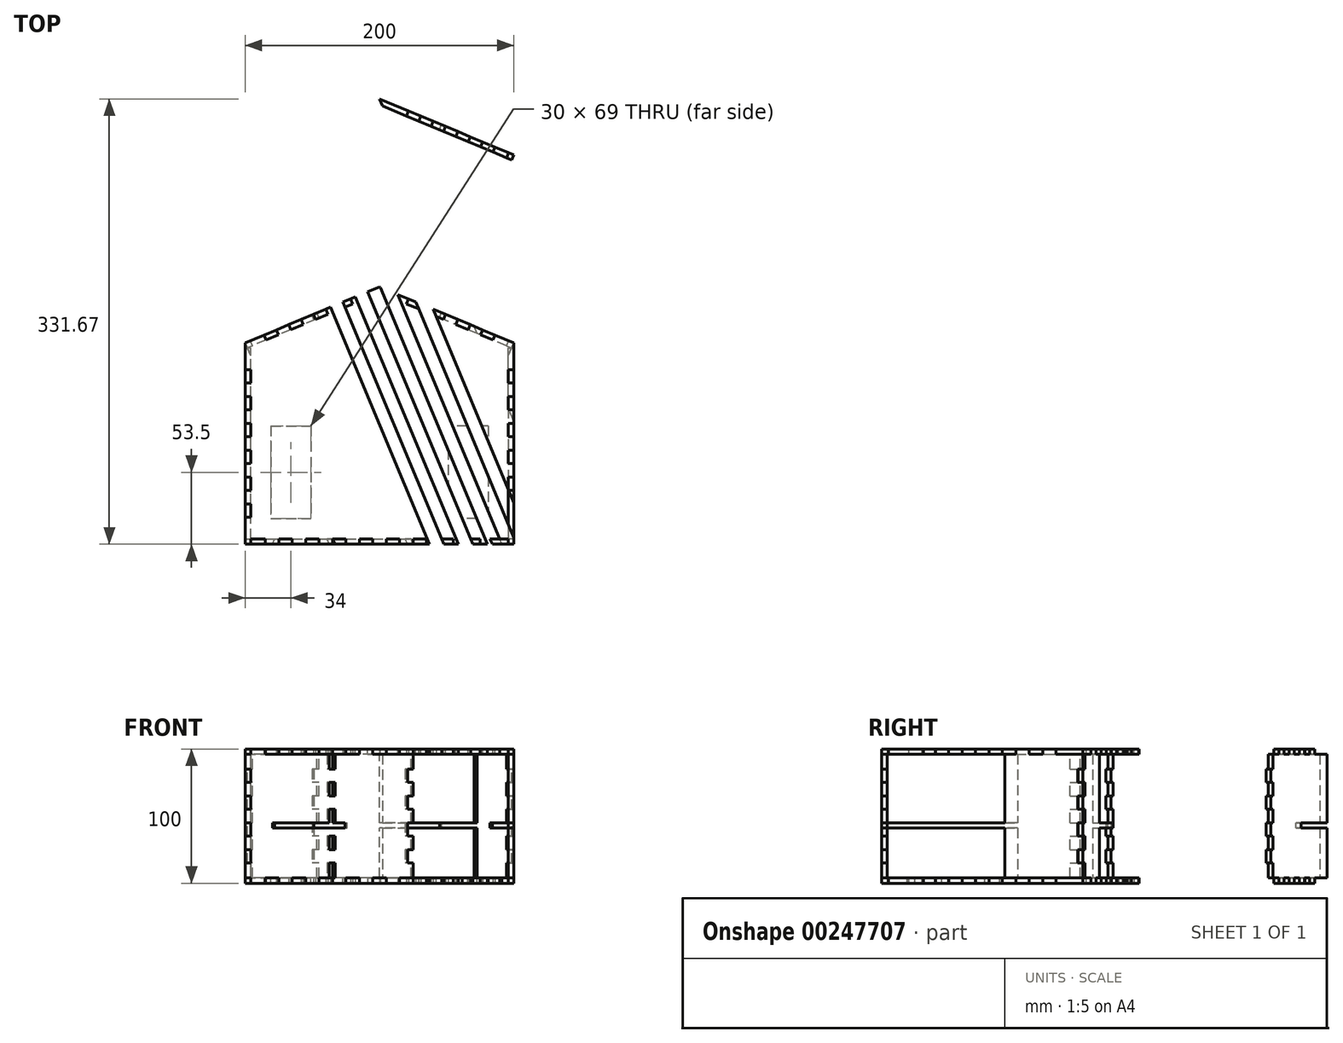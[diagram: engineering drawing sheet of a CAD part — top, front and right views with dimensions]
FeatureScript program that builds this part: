
annotation { "Feature Type Name" : "Feature", "Feature Type Description" : "" }
export const myFeature = defineFeature(function(context is Context, id is Id, definition is map)
    precondition{}
    {
        {
            var Q0;
            Q0=qCreatedBy(makeId("Top.planeOp"),FACE);
            var sketch = newSketch(context, id + "F0", { "sketchPlane" : qUnion([Q0])});
            skLineSegment(sketch, "E0.bottom", {"start": v(100, -100) * mm, "end": v(-100, -100) * mm, "construction": true});
            skLineSegment(sketch, "E0.top", {"start": v(100, 100) * mm, "end": v(-100, 100) * mm, "construction": true});
            skLineSegment(sketch, "E0.left", {"start": v(100, -100) * mm, "end": v(100, 100) * mm, "construction": true});
            skPoint(sketch, "E0.middle", {"position": v(0, 0) * mm});
            skLineSegment(sketch, "E1.bottom", {"start": v(-100, 50) * mm, "end": v(100, 50) * mm});
            skLineSegment(sketch, "E1.top", {"start": v(-100, -100) * mm, "end": v(100, -100) * mm});
            skLineSegment(sketch, "E1.left", {"start": v(-100, 50) * mm, "end": v(-100, -100) * mm});
            skLineSegment(sketch, "E1.right", {"start": v(100, 50) * mm, "end": v(100, -100) * mm});
            skCircle(sketch, "E2", {"center": v(0, 70) * mm, "radius": 20 * mm});
            skLineSegment(sketch, "E3", {"start": v(-100, 100) * mm, "end": v(-100, -100) * mm, "construction": true});
            skLineSegment(sketch, "E4", {"start": v(-100, 50) * mm, "end": v(-7.7, 88.46) * mm});
            skLineSegment(sketch, "E5", {"start": v(7.7, 88.46) * mm, "end": v(100, 50) * mm});
            skLineSegment(sketch, "E6", {"start": v(-100, -25) * mm, "end": v(-96, -25) * mm});
            skLineSegment(sketch, "E7", {"start": v(-96, -100) * mm, "end": v(-96, 50) * mm});
            skLineSegment(sketch, "E8", {"start": v(-100, -30) * mm, "end": v(-96, -30) * mm});
            skLineSegment(sketch, "E9.MirrorCS", {"start": v(-100, -20) * mm, "end": v(-96, -20) * mm});
            skLineSegment(sketch, "E10.direction2", {"start": v(-100, -10) * mm, "end": v(-100, -30) * mm, "construction": true});
            skLineSegment(sketch, "E11.0.1.0", {"start": v(-100, -45) * mm, "end": v(-96, -45) * mm});
            skLineSegment(sketch, "E11.0.1.1", {"start": v(-100, -50) * mm, "end": v(-96, -50) * mm});
            skLineSegment(sketch, "E11.0.1.2", {"start": v(-100, -40) * mm, "end": v(-96, -40) * mm});
            skLineSegment(sketch, "E11.0.2.0", {"start": v(-100, -65) * mm, "end": v(-96, -65) * mm});
            skLineSegment(sketch, "E11.0.2.1", {"start": v(-100, -70) * mm, "end": v(-96, -70) * mm});
            skLineSegment(sketch, "E11.0.2.2", {"start": v(-100, -60) * mm, "end": v(-96, -60) * mm});
            skLineSegment(sketch, "E11.0.3.0", {"start": v(-100, -85) * mm, "end": v(-96, -85) * mm});
            skLineSegment(sketch, "E11.0.3.1", {"start": v(-100, -90) * mm, "end": v(-96, -90) * mm});
            skLineSegment(sketch, "E11.0.3.2", {"start": v(-100, -80) * mm, "end": v(-96, -80) * mm});
            skLineSegment(sketch, "E11.direction1", {"start": v(-100, -30) * mm, "end": v(-75, -30) * mm, "construction": true});
            skLineSegment(sketch, "E11.direction2", {"start": v(-100, -30) * mm, "end": v(-100, -50) * mm, "construction": true});
            skLineSegment(sketch, "E12", {"start": v(100, -25) * mm, "end": v(-100, -25) * mm, "construction": true});
            skLineSegment(sketch, "E13.MirrorCS", {"start": v(-100, 15) * mm, "end": v(-96, 15) * mm});
            skLineSegment(sketch, "E14.MirrorCS", {"start": v(-100, 40) * mm, "end": v(-96, 40) * mm});
            skLineSegment(sketch, "E15.MirrorCS", {"start": v(-100, 20) * mm, "end": v(-96, 20) * mm});
            skLineSegment(sketch, "E16.MirrorCS", {"start": v(-100, 0) * mm, "end": v(-96, 0) * mm});
            skLineSegment(sketch, "E17.MirrorCS", {"start": v(-100, -10) * mm, "end": v(-96, -10) * mm});
            skLineSegment(sketch, "E18.MirrorCS", {"start": v(-100, 10) * mm, "end": v(-96, 10) * mm});
            skLineSegment(sketch, "E19.MirrorCS", {"start": v(-100, -5) * mm, "end": v(-96, -5) * mm});
            skLineSegment(sketch, "E20.MirrorCS", {"start": v(-100, 35) * mm, "end": v(-96, 35) * mm});
            skLineSegment(sketch, "E21.MirrorCS", {"start": v(-100, 30) * mm, "end": v(-96, 30) * mm});
            skLineSegment(sketch, "E22", {"start": v(0, -100) * mm, "end": v(0, 90) * mm, "construction": true});
            skLineSegment(sketch, "E23.MirrorCS", {"start": v(96, -100) * mm, "end": v(96, 50) * mm});
            skLineSegment(sketch, "E24.MirrorCS", {"start": v(100, -5) * mm, "end": v(96, -5) * mm});
            skLineSegment(sketch, "E25.MirrorCS", {"start": v(100, -30) * mm, "end": v(96, -30) * mm});
            skLineSegment(sketch, "E26.MirrorCS", {"start": v(100, -20) * mm, "end": v(96, -20) * mm});
            skLineSegment(sketch, "E27.MirrorCS", {"start": v(100, -80) * mm, "end": v(96, -80) * mm});
            skLineSegment(sketch, "E28.MirrorCS", {"start": v(100, 40) * mm, "end": v(96, 40) * mm});
            skLineSegment(sketch, "E29.MirrorCS", {"start": v(100, 30) * mm, "end": v(96, 30) * mm});
            skLineSegment(sketch, "E30.MirrorCS", {"start": v(100, 35) * mm, "end": v(96, 35) * mm});
            skLineSegment(sketch, "E31.MirrorCS", {"start": v(100, -90) * mm, "end": v(96, -90) * mm});
            skLineSegment(sketch, "E32.MirrorCS", {"start": v(100, -60) * mm, "end": v(96, -60) * mm});
            skLineSegment(sketch, "E33.MirrorCS", {"start": v(100, -10) * mm, "end": v(96, -10) * mm});
            skLineSegment(sketch, "E34.MirrorCS", {"start": v(100, -40) * mm, "end": v(96, -40) * mm});
            skLineSegment(sketch, "E35.MirrorCS", {"start": v(100, 0) * mm, "end": v(96, 0) * mm});
            skLineSegment(sketch, "E36.MirrorCS", {"start": v(100, -65) * mm, "end": v(96, -65) * mm});
            skLineSegment(sketch, "E37.MirrorCS", {"start": v(100, -85) * mm, "end": v(96, -85) * mm});
            skLineSegment(sketch, "E38.MirrorCS", {"start": v(100, -70) * mm, "end": v(96, -70) * mm});
            skLineSegment(sketch, "E39.MirrorCS", {"start": v(100, 10) * mm, "end": v(96, 10) * mm});
            skLineSegment(sketch, "E40.MirrorCS", {"start": v(100, -45) * mm, "end": v(96, -45) * mm});
            skLineSegment(sketch, "E41.MirrorCS", {"start": v(100, -25) * mm, "end": v(96, -25) * mm});
            skLineSegment(sketch, "E42.MirrorCS", {"start": v(100, 15) * mm, "end": v(96, 15) * mm});
            skLineSegment(sketch, "E43.MirrorCS", {"start": v(100, 20) * mm, "end": v(96, 20) * mm});
            skLineSegment(sketch, "E44.MirrorCS", {"start": v(100, -50) * mm, "end": v(96, -50) * mm});
            skLineSegment(sketch, "E45.MirrorCS", {"start": v(100, -10) * mm, "end": v(100, -30) * mm, "construction": true});
            skLineSegment(sketch, "E46.MirrorCS", {"start": v(100, -30) * mm, "end": v(100, -50) * mm, "construction": true});
            skLineSegment(sketch, "E47.MirrorCS", {"start": v(100, -30) * mm, "end": v(75, -30) * mm, "construction": true});
            skLineSegment(sketch, "E48", {"start": v(0, -100) * mm, "end": v(0, -96) * mm});
            skLineSegment(sketch, "E49", {"start": v(0, -96) * mm, "end": v(-96, -96) * mm});
            skLineSegment(sketch, "E50.MirrorCS", {"start": v(0, -96) * mm, "end": v(96, -96) * mm});
            skLineSegment(sketch, "E51", {"start": v(5, -100) * mm, "end": v(5, -96) * mm});
            skLineSegment(sketch, "E52.MirrorCS", {"start": v(-5, -100) * mm, "end": v(-5, -96) * mm});
            skLineSegment(sketch, "E53.1.0.0", {"start": v(15, -100) * mm, "end": v(15, -96) * mm});
            skLineSegment(sketch, "E53.1.0.1", {"start": v(20, -100) * mm, "end": v(20, -96) * mm});
            skLineSegment(sketch, "E53.1.0.2", {"start": v(25, -100) * mm, "end": v(25, -96) * mm});
            skLineSegment(sketch, "E53.2.0.0", {"start": v(35, -100) * mm, "end": v(35, -96) * mm});
            skLineSegment(sketch, "E53.2.0.1", {"start": v(40, -100) * mm, "end": v(40, -96) * mm});
            skLineSegment(sketch, "E53.2.0.2", {"start": v(45, -100) * mm, "end": v(45, -96) * mm});
            skLineSegment(sketch, "E53.3.0.0", {"start": v(55, -100) * mm, "end": v(55, -96) * mm});
            skLineSegment(sketch, "E53.3.0.1", {"start": v(60, -100) * mm, "end": v(60, -96) * mm});
            skLineSegment(sketch, "E53.3.0.2", {"start": v(65, -100) * mm, "end": v(65, -96) * mm});
            skLineSegment(sketch, "E53.4.0.0", {"start": v(75, -100) * mm, "end": v(75, -96) * mm});
            skLineSegment(sketch, "E53.4.0.1", {"start": v(80, -100) * mm, "end": v(80, -96) * mm});
            skLineSegment(sketch, "E53.4.0.2", {"start": v(85, -100) * mm, "end": v(85, -96) * mm});
            skLineSegment(sketch, "E53.direction1", {"start": v(-5, -100) * mm, "end": v(15, -100) * mm, "construction": true});
            skLineSegment(sketch, "E54.MirrorCS", {"start": v(-45, -100) * mm, "end": v(-45, -96) * mm});
            skLineSegment(sketch, "E55.MirrorCS", {"start": v(-40, -100) * mm, "end": v(-40, -96) * mm});
            skLineSegment(sketch, "E56.MirrorCS", {"start": v(-55, -100) * mm, "end": v(-55, -96) * mm});
            skLineSegment(sketch, "E57.MirrorCS", {"start": v(-25, -100) * mm, "end": v(-25, -96) * mm});
            skLineSegment(sketch, "E58.MirrorCS", {"start": v(-85, -100) * mm, "end": v(-85, -96) * mm});
            skLineSegment(sketch, "E59.MirrorCS", {"start": v(-60, -100) * mm, "end": v(-60, -96) * mm});
            skLineSegment(sketch, "E60.MirrorCS", {"start": v(-75, -100) * mm, "end": v(-75, -96) * mm});
            skLineSegment(sketch, "E61.MirrorCS", {"start": v(-15, -100) * mm, "end": v(-15, -96) * mm});
            skLineSegment(sketch, "E62.MirrorCS", {"start": v(-65, -100) * mm, "end": v(-65, -96) * mm});
            skLineSegment(sketch, "E63.MirrorCS", {"start": v(-80, -100) * mm, "end": v(-80, -96) * mm});
            skLineSegment(sketch, "E64.MirrorCS", {"start": v(-20, -100) * mm, "end": v(-20, -96) * mm});
            skLineSegment(sketch, "E65.MirrorCS", {"start": v(-35, -100) * mm, "end": v(-35, -96) * mm});
            skLineSegment(sketch, "E66", {"start": v(-53.85, 69.23) * mm, "end": v(-52.3, 65.54) * mm});
            skLineSegment(sketch, "E67", {"start": v(-52.3, 65.54) * mm, "end": v(-100, 45.67) * mm});
            skLineSegment(sketch, "E68.MirrorCS", {"start": v(-52.3, 65.54) * mm, "end": v(-4.62, 85.41) * mm});
            skLineSegment(sketch, "E69", {"start": v(-58.46, 67.3) * mm, "end": v(-56.92, 63.62) * mm});
            skLineSegment(sketch, "E70.MirrorCS", {"start": v(-49.23, 71.15) * mm, "end": v(-47.7, 67.46) * mm});
            skLineSegment(sketch, "E71.1.0.0", {"start": v(-67.7, 63.46) * mm, "end": v(-66.15, 59.77) * mm});
            skLineSegment(sketch, "E71.1.0.1", {"start": v(-76.92, 59.62) * mm, "end": v(-75.38, 55.92) * mm});
            skLineSegment(sketch, "E71.1.0.2", {"start": v(-72.3, 61.54) * mm, "end": v(-70.77, 57.85) * mm});
            skLineSegment(sketch, "E71.direction1", {"start": v(-75.38, 55.92) * mm, "end": v(-56.92, 63.62) * mm, "construction": true});
            skLineSegment(sketch, "E72.0.2.0", {"start": v(-86.15, 55.77) * mm, "end": v(-84.62, 52.08) * mm});
            skLineSegment(sketch, "E72.3.2.0", {"start": v(-95.38, 51.92) * mm, "end": v(-93.85, 48.23) * mm});
            skLineSegment(sketch, "E72.6.2.0", {"start": v(-90.77, 53.85) * mm, "end": v(-89.23, 50.15) * mm});
            skLineSegment(sketch, "E73.MirrorCS", {"start": v(-12.3, 86.54) * mm, "end": v(-10.77, 82.85) * mm});
            skLineSegment(sketch, "E74.MirrorCS", {"start": v(-16.92, 84.62) * mm, "end": v(-15.38, 80.92) * mm});
            skLineSegment(sketch, "E75.MirrorCS", {"start": v(-30.77, 78.85) * mm, "end": v(-29.23, 75.15) * mm});
            skLineSegment(sketch, "E76.MirrorCS", {"start": v(-40, 75) * mm, "end": v(-38.46, 71.3) * mm});
            skLineSegment(sketch, "E77.MirrorCS", {"start": v(-35.38, 76.92) * mm, "end": v(-33.85, 73.23) * mm});
            skLineSegment(sketch, "E78.MirrorCS", {"start": v(-21.54, 82.7) * mm, "end": v(-20, 79) * mm});
            skLineSegment(sketch, "E79.MirrorCS", {"start": v(21.54, 82.7) * mm, "end": v(20, 79) * mm});
            skLineSegment(sketch, "E80.MirrorCS", {"start": v(40, 75) * mm, "end": v(38.46, 71.3) * mm});
            skLineSegment(sketch, "E81.MirrorCS", {"start": v(53.85, 69.23) * mm, "end": v(52.3, 65.54) * mm});
            skLineSegment(sketch, "E82.MirrorCS", {"start": v(35.38, 76.92) * mm, "end": v(33.85, 73.23) * mm});
            skLineSegment(sketch, "E83.MirrorCS", {"start": v(30.77, 78.85) * mm, "end": v(29.23, 75.15) * mm});
            skLineSegment(sketch, "E84.MirrorCS", {"start": v(16.92, 84.62) * mm, "end": v(15.38, 80.92) * mm});
            skLineSegment(sketch, "E85.MirrorCS", {"start": v(12.3, 86.54) * mm, "end": v(10.77, 82.85) * mm});
            skLineSegment(sketch, "E86.MirrorCS", {"start": v(90.77, 53.85) * mm, "end": v(89.23, 50.15) * mm});
            skLineSegment(sketch, "E87.MirrorCS", {"start": v(95.38, 51.92) * mm, "end": v(93.85, 48.23) * mm});
            skLineSegment(sketch, "E88.MirrorCS", {"start": v(86.15, 55.77) * mm, "end": v(84.62, 52.08) * mm});
            skLineSegment(sketch, "E89.MirrorCS", {"start": v(75.38, 55.92) * mm, "end": v(56.92, 63.62) * mm, "construction": true});
            skLineSegment(sketch, "E90.MirrorCS", {"start": v(72.3, 61.54) * mm, "end": v(70.77, 57.85) * mm});
            skLineSegment(sketch, "E91.MirrorCS", {"start": v(76.92, 59.62) * mm, "end": v(75.38, 55.92) * mm});
            skLineSegment(sketch, "E92.MirrorCS", {"start": v(67.7, 63.46) * mm, "end": v(66.15, 59.77) * mm});
            skLineSegment(sketch, "E93.MirrorCS", {"start": v(58.46, 67.3) * mm, "end": v(56.92, 63.62) * mm});
            skLineSegment(sketch, "E94.MirrorCS", {"start": v(49.23, 71.15) * mm, "end": v(47.7, 67.46) * mm});
            skLineSegment(sketch, "E95.MirrorCS", {"start": v(52.3, 65.54) * mm, "end": v(100, 45.67) * mm});
            skLineSegment(sketch, "E96.MirrorCS", {"start": v(52.3, 65.54) * mm, "end": v(4.62, 85.41) * mm});
            skLineSegment(sketch, "E97", {"start": v(100, 50) * mm, "end": v(96, 47.33) * mm});
            skLineSegment(sketch, "E98", {"start": v(-96, -96) * mm, "end": v(-100, -96) * mm});
            skLineSegment(sketch, "E99", {"start": v(96, -96) * mm, "end": v(100, -96) * mm});
            skLineSegment(sketch, "E100", {"start": v(4.62, 85.41) * mm, "end": v(-4.62, 85.41) * mm});
            skLineSegment(sketch, "E101", {"start": v(7.7, 88.46) * mm, "end": v(0, 91.67) * mm});
            skLineSegment(sketch, "E102", {"start": v(0, 91.67) * mm, "end": v(-7.7, 88.46) * mm});
            skPoint(sketch, "E103.endSnap0", {"position": v(0, 85.41) * mm});
            skLineSegment(sketch, "E104", {"start": v(4.62, 85.41) * mm, "end": v(0, 87.33) * mm});
            skLineSegment(sketch, "E105", {"start": v(0, 87.33) * mm, "end": v(-4.62, 85.41) * mm});
            skSolve(sketch);
        }
        {
            var Q0;
            {var subQ0=sQuery(id+"F0.wireOp",EDGE,"E58.MirrorCS");Q0=makeQuery(id+"F0.imprint","IMPRINT",FACE,{"disambiguationData":[TD([[makeQuery(id+"F0.imprint","IMPRINT",EDGE,{"derivedFrom":subQ0}),-1.0]])]});}
            var Q1;
            {var subQ0=sQuery(id+"F0.wireOp",EDGE,"E60.MirrorCS");Q1=makeQuery(id+"F0.imprint","IMPRINT",FACE,{"disambiguationData":[TD([[makeQuery(id+"F0.imprint","IMPRINT",EDGE,{"derivedFrom":subQ0}),1.0]])]});}
            var Q2;
            {var subQ0=sQuery(id+"F0.wireOp",EDGE,"E59.MirrorCS");Q2=makeQuery(id+"F0.imprint","IMPRINT",FACE,{"disambiguationData":[TD([[makeQuery(id+"F0.imprint","IMPRINT",EDGE,{"derivedFrom":subQ0}),1.0]])]});}
            var Q3;
            {var subQ0=sQuery(id+"F0.wireOp",EDGE,"E56.MirrorCS");Q3=makeQuery(id+"F0.imprint","IMPRINT",FACE,{"disambiguationData":[TD([[makeQuery(id+"F0.imprint","IMPRINT",EDGE,{"derivedFrom":subQ0}),1.0]])]});}
            var Q4;
            {var subQ0=sQuery(id+"F0.wireOp",EDGE,"E54.MirrorCS");Q4=makeQuery(id+"F0.imprint","IMPRINT",FACE,{"disambiguationData":[TD([[makeQuery(id+"F0.imprint","IMPRINT",EDGE,{"derivedFrom":subQ0}),-1.0]])]});}
            var Q5;
            {var subQ0=sQuery(id+"F0.wireOp",EDGE,"E55.MirrorCS");Q5=makeQuery(id+"F0.imprint","IMPRINT",FACE,{"disambiguationData":[TD([[makeQuery(id+"F0.imprint","IMPRINT",EDGE,{"derivedFrom":subQ0}),-1.0]])]});}
            var Q6;
            {var subQ0=sQuery(id+"F0.wireOp",EDGE,"E57.MirrorCS");Q6=makeQuery(id+"F0.imprint","IMPRINT",FACE,{"disambiguationData":[TD([[makeQuery(id+"F0.imprint","IMPRINT",EDGE,{"derivedFrom":subQ0}),-1.0]])]});}
            var Q7;
            {var subQ0=sQuery(id+"F0.wireOp",EDGE,"E61.MirrorCS");Q7=makeQuery(id+"F0.imprint","IMPRINT",FACE,{"disambiguationData":[TD([[makeQuery(id+"F0.imprint","IMPRINT",EDGE,{"derivedFrom":subQ0}),1.0]])]});}
            var Q8;
            {var subQ0=sQuery(id+"F0.wireOp",EDGE,"E48");Q8=makeQuery(id+"F0.imprint","IMPRINT",FACE,{"disambiguationData":[TD([[makeQuery(id+"F0.imprint","IMPRINT",EDGE,{"derivedFrom":subQ0}),1.0]])]});}
            var Q9;
            {var subQ0=sQuery(id+"F0.wireOp",EDGE,"E48");Q9=makeQuery(id+"F0.imprint","IMPRINT",FACE,{"disambiguationData":[TD([[makeQuery(id+"F0.imprint","IMPRINT",EDGE,{"derivedFrom":subQ0}),-1.0]])]});}
            var Q10;
            {var subQ0=sQuery(id+"F0.wireOp",EDGE,"E53.1.0.0");Q10=makeQuery(id+"F0.imprint","IMPRINT",FACE,{"disambiguationData":[TD([[makeQuery(id+"F0.imprint","IMPRINT",EDGE,{"derivedFrom":subQ0}),-1.0]])]});}
            var Q11;
            {var subQ0=sQuery(id+"F0.wireOp",EDGE,"E53.1.0.1");Q11=makeQuery(id+"F0.imprint","IMPRINT",FACE,{"disambiguationData":[TD([[makeQuery(id+"F0.imprint","IMPRINT",EDGE,{"derivedFrom":subQ0}),-1.0]])]});}
            var Q12;
            {var subQ0=sQuery(id+"F0.wireOp",EDGE,"E53.2.0.0");Q12=makeQuery(id+"F0.imprint","IMPRINT",FACE,{"disambiguationData":[TD([[makeQuery(id+"F0.imprint","IMPRINT",EDGE,{"derivedFrom":subQ0}),-1.0]])]});}
            var Q13;
            {var subQ0=sQuery(id+"F0.wireOp",EDGE,"E53.2.0.1");Q13=makeQuery(id+"F0.imprint","IMPRINT",FACE,{"disambiguationData":[TD([[makeQuery(id+"F0.imprint","IMPRINT",EDGE,{"derivedFrom":subQ0}),-1.0]])]});}
            var Q14;
            {var subQ0=sQuery(id+"F0.wireOp",EDGE,"E53.3.0.0");Q14=makeQuery(id+"F0.imprint","IMPRINT",FACE,{"disambiguationData":[TD([[makeQuery(id+"F0.imprint","IMPRINT",EDGE,{"derivedFrom":subQ0}),-1.0]])]});}
            var Q15;
            {var subQ0=sQuery(id+"F0.wireOp",EDGE,"E53.3.0.1");Q15=makeQuery(id+"F0.imprint","IMPRINT",FACE,{"disambiguationData":[TD([[makeQuery(id+"F0.imprint","IMPRINT",EDGE,{"derivedFrom":subQ0}),-1.0]])]});}
            var Q16;
            {var subQ0=sQuery(id+"F0.wireOp",EDGE,"E53.4.0.0");Q16=makeQuery(id+"F0.imprint","IMPRINT",FACE,{"disambiguationData":[TD([[makeQuery(id+"F0.imprint","IMPRINT",EDGE,{"derivedFrom":subQ0}),-1.0]])]});}
            var Q17;
            {var subQ0=sQuery(id+"F0.wireOp",EDGE,"E53.4.0.1");Q17=makeQuery(id+"F0.imprint","IMPRINT",FACE,{"disambiguationData":[TD([[makeQuery(id+"F0.imprint","IMPRINT",EDGE,{"derivedFrom":subQ0}),-1.0]])]});}
            var Q18;
            {var subQ0=sQuery(id+"F0.wireOp",EDGE,"E14.MirrorCS");Q18=makeQuery(id+"F0.imprint","IMPRINT",FACE,{"disambiguationData":[TD([[makeQuery(id+"F0.imprint","IMPRINT",EDGE,{"derivedFrom":subQ0}),-1.0]])]});}
            var Q19;
            {var subQ0=sQuery(id+"F0.wireOp",EDGE,"E20.MirrorCS");Q19=makeQuery(id+"F0.imprint","IMPRINT",FACE,{"disambiguationData":[TD([[makeQuery(id+"F0.imprint","IMPRINT",EDGE,{"derivedFrom":subQ0}),-1.0]])]});}
            var Q20;
            {var subQ0=sQuery(id+"F0.wireOp",EDGE,"E13.MirrorCS");Q20=makeQuery(id+"F0.imprint","IMPRINT",FACE,{"disambiguationData":[TD([[makeQuery(id+"F0.imprint","IMPRINT",EDGE,{"derivedFrom":subQ0}),1.0]])]});}
            var Q21;
            {var subQ0=sQuery(id+"F0.wireOp",EDGE,"E13.MirrorCS");Q21=makeQuery(id+"F0.imprint","IMPRINT",FACE,{"disambiguationData":[TD([[makeQuery(id+"F0.imprint","IMPRINT",EDGE,{"derivedFrom":subQ0}),-1.0]])]});}
            var Q22;
            {var subQ0=sQuery(id+"F0.wireOp",EDGE,"E16.MirrorCS");Q22=makeQuery(id+"F0.imprint","IMPRINT",FACE,{"disambiguationData":[TD([[makeQuery(id+"F0.imprint","IMPRINT",EDGE,{"derivedFrom":subQ0}),-1.0]])]});}
            var Q23;
            {var subQ0=sQuery(id+"F0.wireOp",EDGE,"E17.MirrorCS");Q23=makeQuery(id+"F0.imprint","IMPRINT",FACE,{"disambiguationData":[TD([[makeQuery(id+"F0.imprint","IMPRINT",EDGE,{"derivedFrom":subQ0}),1.0]])]});}
            var Q24;
            {var subQ0=sQuery(id+"F0.wireOp",EDGE,"E6");Q24=makeQuery(id+"F0.imprint","IMPRINT",FACE,{"disambiguationData":[TD([[makeQuery(id+"F0.imprint","IMPRINT",EDGE,{"derivedFrom":subQ0}),1.0]])]});}
            var Q25;
            {var subQ0=sQuery(id+"F0.wireOp",EDGE,"E6");Q25=makeQuery(id+"F0.imprint","IMPRINT",FACE,{"disambiguationData":[TD([[makeQuery(id+"F0.imprint","IMPRINT",EDGE,{"derivedFrom":subQ0}),-1.0]])]});}
            var Q26;
            {var subQ0=sQuery(id+"F0.wireOp",EDGE,"E11.0.1.0");Q26=makeQuery(id+"F0.imprint","IMPRINT",FACE,{"disambiguationData":[TD([[makeQuery(id+"F0.imprint","IMPRINT",EDGE,{"derivedFrom":subQ0}),1.0]])]});}
            var Q27;
            {var subQ0=sQuery(id+"F0.wireOp",EDGE,"E11.0.1.0");Q27=makeQuery(id+"F0.imprint","IMPRINT",FACE,{"disambiguationData":[TD([[makeQuery(id+"F0.imprint","IMPRINT",EDGE,{"derivedFrom":subQ0}),-1.0]])]});}
            var Q28;
            {var subQ0=sQuery(id+"F0.wireOp",EDGE,"E11.0.2.0");Q28=makeQuery(id+"F0.imprint","IMPRINT",FACE,{"disambiguationData":[TD([[makeQuery(id+"F0.imprint","IMPRINT",EDGE,{"derivedFrom":subQ0}),1.0]])]});}
            var Q29;
            {var subQ0=sQuery(id+"F0.wireOp",EDGE,"E11.0.2.0");Q29=makeQuery(id+"F0.imprint","IMPRINT",FACE,{"disambiguationData":[TD([[makeQuery(id+"F0.imprint","IMPRINT",EDGE,{"derivedFrom":subQ0}),-1.0]])]});}
            var Q30;
            {var subQ0=sQuery(id+"F0.wireOp",EDGE,"E11.0.3.0");Q30=makeQuery(id+"F0.imprint","IMPRINT",FACE,{"disambiguationData":[TD([[makeQuery(id+"F0.imprint","IMPRINT",EDGE,{"derivedFrom":subQ0}),1.0]])]});}
            var Q31;
            {var subQ0=sQuery(id+"F0.wireOp",EDGE,"E11.0.3.0");Q31=makeQuery(id+"F0.imprint","IMPRINT",FACE,{"disambiguationData":[TD([[makeQuery(id+"F0.imprint","IMPRINT",EDGE,{"derivedFrom":subQ0}),-1.0]])]});}
            var Q32;
            {var subQ0=sQuery(id+"F0.wireOp",EDGE,"E28.MirrorCS");Q32=makeQuery(id+"F0.imprint","IMPRINT",FACE,{"disambiguationData":[TD([[makeQuery(id+"F0.imprint","IMPRINT",EDGE,{"derivedFrom":subQ0}),1.0]])]});}
            var Q33;
            {var subQ0=sQuery(id+"F0.wireOp",EDGE,"E29.MirrorCS");Q33=makeQuery(id+"F0.imprint","IMPRINT",FACE,{"disambiguationData":[TD([[makeQuery(id+"F0.imprint","IMPRINT",EDGE,{"derivedFrom":subQ0}),-1.0]])]});}
            var Q34;
            {var subQ0=sQuery(id+"F0.wireOp",EDGE,"E42.MirrorCS");Q34=makeQuery(id+"F0.imprint","IMPRINT",FACE,{"disambiguationData":[TD([[makeQuery(id+"F0.imprint","IMPRINT",EDGE,{"derivedFrom":subQ0}),-1.0]])]});}
            var Q35;
            {var subQ0=sQuery(id+"F0.wireOp",EDGE,"E39.MirrorCS");Q35=makeQuery(id+"F0.imprint","IMPRINT",FACE,{"disambiguationData":[TD([[makeQuery(id+"F0.imprint","IMPRINT",EDGE,{"derivedFrom":subQ0}),-1.0]])]});}
            var Q36;
            {var subQ0=sQuery(id+"F0.wireOp",EDGE,"E24.MirrorCS");Q36=makeQuery(id+"F0.imprint","IMPRINT",FACE,{"disambiguationData":[TD([[makeQuery(id+"F0.imprint","IMPRINT",EDGE,{"derivedFrom":subQ0}),-1.0]])]});}
            var Q37;
            {var subQ0=sQuery(id+"F0.wireOp",EDGE,"E24.MirrorCS");Q37=makeQuery(id+"F0.imprint","IMPRINT",FACE,{"disambiguationData":[TD([[makeQuery(id+"F0.imprint","IMPRINT",EDGE,{"derivedFrom":subQ0}),1.0]])]});}
            var Q38;
            {var subQ0=sQuery(id+"F0.wireOp",EDGE,"E26.MirrorCS");Q38=makeQuery(id+"F0.imprint","IMPRINT",FACE,{"disambiguationData":[TD([[makeQuery(id+"F0.imprint","IMPRINT",EDGE,{"derivedFrom":subQ0}),1.0]])]});}
            var Q39;
            {var subQ0=sQuery(id+"F0.wireOp",EDGE,"E25.MirrorCS");Q39=makeQuery(id+"F0.imprint","IMPRINT",FACE,{"disambiguationData":[TD([[makeQuery(id+"F0.imprint","IMPRINT",EDGE,{"derivedFrom":subQ0}),-1.0]])]});}
            var Q40;
            {var subQ0=sQuery(id+"F0.wireOp",EDGE,"E34.MirrorCS");Q40=makeQuery(id+"F0.imprint","IMPRINT",FACE,{"disambiguationData":[TD([[makeQuery(id+"F0.imprint","IMPRINT",EDGE,{"derivedFrom":subQ0}),1.0]])]});}
            var Q41;
            {var subQ0=sQuery(id+"F0.wireOp",EDGE,"E40.MirrorCS");Q41=makeQuery(id+"F0.imprint","IMPRINT",FACE,{"disambiguationData":[TD([[makeQuery(id+"F0.imprint","IMPRINT",EDGE,{"derivedFrom":subQ0}),1.0]])]});}
            var Q42;
            {var subQ0=sQuery(id+"F0.wireOp",EDGE,"E32.MirrorCS");Q42=makeQuery(id+"F0.imprint","IMPRINT",FACE,{"disambiguationData":[TD([[makeQuery(id+"F0.imprint","IMPRINT",EDGE,{"derivedFrom":subQ0}),1.0]])]});}
            var Q43;
            {var subQ0=sQuery(id+"F0.wireOp",EDGE,"E36.MirrorCS");Q43=makeQuery(id+"F0.imprint","IMPRINT",FACE,{"disambiguationData":[TD([[makeQuery(id+"F0.imprint","IMPRINT",EDGE,{"derivedFrom":subQ0}),1.0]])]});}
            var Q44;
            {var subQ0=sQuery(id+"F0.wireOp",EDGE,"E27.MirrorCS");Q44=makeQuery(id+"F0.imprint","IMPRINT",FACE,{"disambiguationData":[TD([[makeQuery(id+"F0.imprint","IMPRINT",EDGE,{"derivedFrom":subQ0}),1.0]])]});}
            var Q45;
            {var subQ0=sQuery(id+"F0.wireOp",EDGE,"E31.MirrorCS");Q45=makeQuery(id+"F0.imprint","IMPRINT",FACE,{"disambiguationData":[TD([[makeQuery(id+"F0.imprint","IMPRINT",EDGE,{"derivedFrom":subQ0}),-1.0]])]});}
            var Q46;
            {var subQ0=sQuery(id+"F0.wireOp",EDGE,"E72.0.2.0");Q46=makeQuery(id+"F0.imprint","IMPRINT",FACE,{"disambiguationData":[TD([[makeQuery(id+"F0.imprint","IMPRINT",EDGE,{"derivedFrom":subQ0}),-1.0]])]});}
            var Q47;
            {var subQ5=sQuery(id+"F0.wireOp",EDGE,"E72.6.2.0");Q47=makeQuery(id+"F0.imprint","IMPRINT",FACE,{"disambiguationData":[TD([[makeQuery(id+"F0.imprint","IMPRINT",EDGE,{"derivedFrom":subQ5}),-1.0]])]});}
            var Q48;
            {var subQ0=sQuery(id+"F0.wireOp",EDGE,"E71.1.0.1");Q48=makeQuery(id+"F0.imprint","IMPRINT",FACE,{"disambiguationData":[TD([[makeQuery(id+"F0.imprint","IMPRINT",EDGE,{"derivedFrom":subQ0}),1.0]])]});}
            var Q49;
            {var subQ0=sQuery(id+"F0.wireOp",EDGE,"E71.1.0.0");Q49=makeQuery(id+"F0.imprint","IMPRINT",FACE,{"disambiguationData":[TD([[makeQuery(id+"F0.imprint","IMPRINT",EDGE,{"derivedFrom":subQ0}),-1.0]])]});}
            var Q50;
            {var subQ0=sQuery(id+"F0.wireOp",EDGE,"E72.3.2.0");var subQ1=sQuery(id+"F0.wireOp",EDGE,"E1.bottom");var subQ2=makeQuery(id+"F0.imprint","INTERSECT",VERTEX,{"derivedFrom":[subQ1,subQ0]});Q50=makeQuery(id+"F0.imprint","IMPRINT",FACE,{"disambiguationData":[TD([[makeQuery(id+"F0.imprint","IMPRINT",EDGE,{"disambiguationData":[TD([[subQ2,-1.0]])],"derivedFrom":subQ1}),-1.0]])]});}
            var Q51;
            {var subQ0=sQuery(id+"F0.wireOp",EDGE,"E66");Q51=makeQuery(id+"F0.imprint","IMPRINT",FACE,{"disambiguationData":[TD([[makeQuery(id+"F0.imprint","IMPRINT",EDGE,{"derivedFrom":subQ0}),-1.0]])]});}
            var Q52;
            {var subQ0=sQuery(id+"F0.wireOp",EDGE,"E66");Q52=makeQuery(id+"F0.imprint","IMPRINT",FACE,{"disambiguationData":[TD([[makeQuery(id+"F0.imprint","IMPRINT",EDGE,{"derivedFrom":subQ0}),1.0]])]});}
            var Q53;
            {var subQ0=sQuery(id+"F0.wireOp",EDGE,"E76.MirrorCS");Q53=makeQuery(id+"F0.imprint","IMPRINT",FACE,{"disambiguationData":[TD([[makeQuery(id+"F0.imprint","IMPRINT",EDGE,{"derivedFrom":subQ0}),1.0]])]});}
            var Q54;
            {var subQ0=sQuery(id+"F0.wireOp",EDGE,"E75.MirrorCS");Q54=makeQuery(id+"F0.imprint","IMPRINT",FACE,{"disambiguationData":[TD([[makeQuery(id+"F0.imprint","IMPRINT",EDGE,{"derivedFrom":subQ0}),-1.0]])]});}
            var Q55;
            {var subQ0=sQuery(id+"F0.wireOp",EDGE,"E78.MirrorCS");Q55=makeQuery(id+"F0.imprint","IMPRINT",FACE,{"disambiguationData":[TD([[makeQuery(id+"F0.imprint","IMPRINT",EDGE,{"derivedFrom":subQ0}),1.0]])]});}
            var Q56;
            {var subQ0=sQuery(id+"F0.wireOp",EDGE,"E73.MirrorCS");var subQ1=sQuery(id+"F0.wireOp",EDGE,"E2");var subQ2=makeQuery(id+"F0.imprint","INTERSECT",VERTEX,{"derivedFrom":[subQ1,subQ0]});Q56=makeQuery(id+"F0.imprint","IMPRINT",FACE,{"disambiguationData":[TD([[makeQuery(id+"F0.imprint","IMPRINT",EDGE,{"disambiguationData":[TD([[subQ2,-1.0]])],"derivedFrom":subQ1}),1.0]])]});}
            var Q57;
            {var subQ0=sQuery(id+"F0.wireOp",EDGE,"E73.MirrorCS");var subQ1=sQuery(id+"F0.wireOp",EDGE,"E2");var subQ2=makeQuery(id+"F0.imprint","INTERSECT",VERTEX,{"derivedFrom":[subQ1,subQ0]});Q57=makeQuery(id+"F0.imprint","IMPRINT",FACE,{"disambiguationData":[TD([[makeQuery(id+"F0.imprint","IMPRINT",EDGE,{"disambiguationData":[TD([[subQ2,-1.0]])],"derivedFrom":subQ1}),-1.0]])]});}
            var Q58;
            {var subQ0=sQuery(id+"F0.wireOp",EDGE,"E84.MirrorCS");var subQ1=sQuery(id+"F0.wireOp",EDGE,"E2");var subQ2=makeQuery(id+"F0.imprint","INTERSECT",VERTEX,{"derivedFrom":[subQ1,subQ0]});Q58=makeQuery(id+"F0.imprint","IMPRINT",FACE,{"disambiguationData":[TD([[makeQuery(id+"F0.imprint","IMPRINT",EDGE,{"disambiguationData":[TD([[subQ2,-1.0]])],"derivedFrom":subQ1}),1.0]])]});}
            var Q59;
            {var subQ0=sQuery(id+"F0.wireOp",EDGE,"E84.MirrorCS");var subQ1=sQuery(id+"F0.wireOp",EDGE,"E2");var subQ2=makeQuery(id+"F0.imprint","INTERSECT",VERTEX,{"derivedFrom":[subQ1,subQ0]});Q59=makeQuery(id+"F0.imprint","IMPRINT",FACE,{"disambiguationData":[TD([[makeQuery(id+"F0.imprint","IMPRINT",EDGE,{"disambiguationData":[TD([[subQ2,-1.0]])],"derivedFrom":subQ1}),-1.0]])]});}
            var Q60;
            {var subQ5=sQuery(id+"F0.wireOp",EDGE,"E79.MirrorCS");Q60=makeQuery(id+"F0.imprint","IMPRINT",FACE,{"disambiguationData":[TD([[makeQuery(id+"F0.imprint","IMPRINT",EDGE,{"derivedFrom":subQ5}),-1.0]])]});}
            var Q61;
            {var subQ0=sQuery(id+"F0.wireOp",EDGE,"E82.MirrorCS");Q61=makeQuery(id+"F0.imprint","IMPRINT",FACE,{"disambiguationData":[TD([[makeQuery(id+"F0.imprint","IMPRINT",EDGE,{"derivedFrom":subQ0}),-1.0]])]});}
            var Q62;
            {var subQ0=sQuery(id+"F0.wireOp",EDGE,"E80.MirrorCS");Q62=makeQuery(id+"F0.imprint","IMPRINT",FACE,{"disambiguationData":[TD([[makeQuery(id+"F0.imprint","IMPRINT",EDGE,{"derivedFrom":subQ0}),-1.0]])]});}
            var Q63;
            {var subQ0=sQuery(id+"F0.wireOp",EDGE,"E84.MirrorCS");var subQ1=sQuery(id+"F0.wireOp",EDGE,"E2");var subQ2=makeQuery(id+"F0.imprint","INTERSECT",VERTEX,{"derivedFrom":[subQ1,subQ0]});Q63=makeQuery(id+"F0.imprint","IMPRINT",FACE,{"disambiguationData":[TD([[makeQuery(id+"F0.imprint","IMPRINT",EDGE,{"disambiguationData":[TD([[subQ2,1.0]])],"derivedFrom":subQ1}),1.0]])]});}
            var Q64;
            {var subQ0=sQuery(id+"F0.wireOp",EDGE,"E74.MirrorCS");var subQ1=sQuery(id+"F0.wireOp",EDGE,"E2");var subQ2=makeQuery(id+"F0.imprint","INTERSECT",VERTEX,{"derivedFrom":[subQ1,subQ0]});Q64=makeQuery(id+"F0.imprint","IMPRINT",FACE,{"disambiguationData":[TD([[makeQuery(id+"F0.imprint","IMPRINT",EDGE,{"disambiguationData":[TD([[subQ2,-1.0]])],"derivedFrom":subQ1}),1.0]])]});}
            var Q65;
            {var subQ0=sQuery(id+"F0.wireOp",EDGE,"E81.MirrorCS");Q65=makeQuery(id+"F0.imprint","IMPRINT",FACE,{"disambiguationData":[TD([[makeQuery(id+"F0.imprint","IMPRINT",EDGE,{"derivedFrom":subQ0}),-1.0]])]});}
            var Q66;
            {var subQ0=sQuery(id+"F0.wireOp",EDGE,"E81.MirrorCS");Q66=makeQuery(id+"F0.imprint","IMPRINT",FACE,{"disambiguationData":[TD([[makeQuery(id+"F0.imprint","IMPRINT",EDGE,{"derivedFrom":subQ0}),1.0]])]});}
            var Q67;
            {var subQ0=sQuery(id+"F0.wireOp",EDGE,"E90.MirrorCS");Q67=makeQuery(id+"F0.imprint","IMPRINT",FACE,{"disambiguationData":[TD([[makeQuery(id+"F0.imprint","IMPRINT",EDGE,{"derivedFrom":subQ0}),-1.0]])]});}
            var Q68;
            {var subQ0=sQuery(id+"F0.wireOp",EDGE,"E90.MirrorCS");Q68=makeQuery(id+"F0.imprint","IMPRINT",FACE,{"disambiguationData":[TD([[makeQuery(id+"F0.imprint","IMPRINT",EDGE,{"derivedFrom":subQ0}),1.0]])]});}
            var Q69;
            {var subQ0=sQuery(id+"F0.wireOp",EDGE,"E86.MirrorCS");Q69=makeQuery(id+"F0.imprint","IMPRINT",FACE,{"disambiguationData":[TD([[makeQuery(id+"F0.imprint","IMPRINT",EDGE,{"derivedFrom":subQ0}),-1.0]])]});}
            var Q70;
            {var subQ5=sQuery(id+"F0.wireOp",EDGE,"E86.MirrorCS");Q70=makeQuery(id+"F0.imprint","IMPRINT",FACE,{"disambiguationData":[TD([[makeQuery(id+"F0.imprint","IMPRINT",EDGE,{"derivedFrom":subQ5}),1.0]])]});}
            var Q71;
            {var subQ8=sQuery(id+"F0.wireOp",EDGE,"E67");var subQ14=sQuery(id+"F0.wireOp",EDGE,"E1.bottom");var subQ15=makeQuery(id+"F0.imprint","INTERSECT",VERTEX,{"derivedFrom":[subQ14,subQ8]});Q71=makeQuery(id+"F0.imprint","IMPRINT",FACE,{"disambiguationData":[TD([[makeQuery(id+"F0.imprint","IMPRINT",EDGE,{"disambiguationData":[TD([[subQ15,-1.0]])],"derivedFrom":subQ14}),-1.0]])]});}
            var Q72;
            {var subQ1=sQuery(id+"F0.wireOp",EDGE,"E67");var subQ5=sQuery(id+"F0.wireOp",EDGE,"E1.bottom");var subQ6=makeQuery(id+"F0.imprint","INTERSECT",VERTEX,{"derivedFrom":[subQ5,subQ1]});Q72=makeQuery(id+"F0.imprint","IMPRINT",FACE,{"disambiguationData":[TD([[makeQuery(id+"F0.imprint","IMPRINT",EDGE,{"disambiguationData":[TD([[subQ6,-1.0]])],"derivedFrom":subQ5}),1.0]])]});}
            var Q73;
            {var subQ2=sQuery(id+"F0.wireOp",EDGE,"E1.bottom");var subQ8=sQuery(id+"F0.wireOp",EDGE,"E2");var subQ9=makeQuery(id+"F0.imprint","INTERSECT",VERTEX,{"derivedFrom":[subQ2,subQ8]});Q73=makeQuery(id+"F0.imprint","IMPRINT",FACE,{"disambiguationData":[TD([[makeQuery(id+"F0.imprint","IMPRINT",EDGE,{"disambiguationData":[TD([[subQ9,-1.0]])],"derivedFrom":subQ2}),1.0]])]});}
            var Q74;
            {var subQ0=sQuery(id+"F0.wireOp",EDGE,"E7");var subQ1=sQuery(id+"F0.wireOp",EDGE,"E1.bottom");var subQ2=makeQuery(id+"F0.imprint","INTERSECT",VERTEX,{"derivedFrom":[subQ1,subQ0]});Q74=makeQuery(id+"F0.imprint","IMPRINT",FACE,{"disambiguationData":[TD([[makeQuery(id+"F0.imprint","IMPRINT",EDGE,{"disambiguationData":[TD([[subQ2,-1.0]])],"derivedFrom":subQ1}),-1.0]])]});}
            var Q75;
            {var subQ1=sQuery(id+"F0.wireOp",EDGE,"E1.bottom");var subQ3=makeQuery(id+"F0.imprint","INTERSECT",VERTEX,{"derivedFrom":[subQ1,sQuery(id+"F0.wireOp",EDGE,"E7")]});Q75=makeQuery(id+"F0.imprint","IMPRINT",FACE,{"disambiguationData":[TD([[makeQuery(id+"F0.imprint","IMPRINT",EDGE,{"disambiguationData":[TD([[subQ3,-1.0]])],"derivedFrom":subQ1}),1.0]])]});}
            var Q76;
            {var subQ1=sQuery(id+"F0.wireOp",EDGE,"E1.bottom");var subQ3=sQuery(id+"F0.wireOp",EDGE,"E7");var subQ4=makeQuery(id+"F0.imprint","INTERSECT",VERTEX,{"derivedFrom":[subQ1,subQ3]});Q76=makeQuery(id+"F0.imprint","IMPRINT",FACE,{"disambiguationData":[TD([[makeQuery(id+"F0.imprint","IMPRINT",EDGE,{"disambiguationData":[TD([[subQ4,1.0]])],"derivedFrom":subQ3}),1.0]])]});}
            var Q77;
            {var subQ0=sQuery(id+"F0.wireOp",EDGE,"E14.MirrorCS");Q77=makeQuery(id+"F0.imprint","IMPRINT",FACE,{"disambiguationData":[TD([[makeQuery(id+"F0.imprint","IMPRINT",EDGE,{"derivedFrom":subQ0}),1.0]])]});}
            var Q78;
            {var subQ0=sQuery(id+"F0.wireOp",EDGE,"E1.bottom");var subQ1=makeQuery(id+"F0.imprint","INTERSECT",VERTEX,{"derivedFrom":[subQ0,sQuery(id+"F0.wireOp",EDGE,"E23.MirrorCS")]});Q78=makeQuery(id+"F0.imprint","IMPRINT",FACE,{"disambiguationData":[TD([[makeQuery(id+"F0.imprint","IMPRINT",EDGE,{"disambiguationData":[TD([[subQ1,1.0]])],"derivedFrom":subQ0}),1.0]])]});}
            var Q79;
            {var subQ0=sQuery(id+"F0.wireOp",EDGE,"E23.MirrorCS");var subQ1=sQuery(id+"F0.wireOp",EDGE,"E1.bottom");var subQ2=makeQuery(id+"F0.imprint","INTERSECT",VERTEX,{"derivedFrom":[subQ1,subQ0]});Q79=makeQuery(id+"F0.imprint","IMPRINT",FACE,{"disambiguationData":[TD([[makeQuery(id+"F0.imprint","IMPRINT",EDGE,{"disambiguationData":[TD([[subQ2,1.0]])],"derivedFrom":subQ1}),-1.0]])]});}
            var Q80;
            {var subQ0=sQuery(id+"F0.wireOp",EDGE,"E95.MirrorCS");var subQ1=sQuery(id+"F0.wireOp",EDGE,"E1.bottom");var subQ2=makeQuery(id+"F0.imprint","INTERSECT",VERTEX,{"derivedFrom":[subQ1,subQ0]});Q80=makeQuery(id+"F0.imprint","IMPRINT",FACE,{"disambiguationData":[TD([[makeQuery(id+"F0.imprint","IMPRINT",EDGE,{"disambiguationData":[TD([[subQ2,-1.0]])],"derivedFrom":subQ1}),-1.0]])]});}
            var Q81;
            {var subQ1=sQuery(id+"F0.wireOp",EDGE,"E1.bottom");var subQ3=sQuery(id+"F0.wireOp",EDGE,"E23.MirrorCS");var subQ4=makeQuery(id+"F0.imprint","INTERSECT",VERTEX,{"derivedFrom":[subQ1,subQ3]});Q81=makeQuery(id+"F0.imprint","IMPRINT",FACE,{"disambiguationData":[TD([[makeQuery(id+"F0.imprint","IMPRINT",EDGE,{"disambiguationData":[TD([[subQ4,1.0]])],"derivedFrom":subQ3}),-1.0]])]});}
            var Q82;
            {var subQ0=sQuery(id+"F0.wireOp",EDGE,"E28.MirrorCS");Q82=makeQuery(id+"F0.imprint","IMPRINT",FACE,{"disambiguationData":[TD([[makeQuery(id+"F0.imprint","IMPRINT",EDGE,{"derivedFrom":subQ0}),-1.0]])]});}
            var Q83;
            {var subQ0=sQuery(id+"F0.wireOp",EDGE,"E97");Q83=makeQuery(id+"F0.imprint","IMPRINT",FACE,{"disambiguationData":[TD([[makeQuery(id+"F0.imprint","IMPRINT",EDGE,{"derivedFrom":subQ0}),1.0]])]});}
            var Q84;
            {var subQ0=sQuery(id+"F0.wireOp",EDGE,"E31.MirrorCS");Q84=makeQuery(id+"F0.imprint","IMPRINT",FACE,{"disambiguationData":[TD([[makeQuery(id+"F0.imprint","IMPRINT",EDGE,{"derivedFrom":subQ0}),1.0]])]});}
            var Q85;
            {var subQ0=sQuery(id+"F0.wireOp",EDGE,"E11.0.3.1");Q85=makeQuery(id+"F0.imprint","IMPRINT",FACE,{"disambiguationData":[TD([[makeQuery(id+"F0.imprint","IMPRINT",EDGE,{"derivedFrom":subQ0}),-1.0]])]});}
            var Q86;
            {var subQ5=sQuery(id+"F0.wireOp",EDGE,"E98");Q86=makeQuery(id+"F0.imprint","IMPRINT",FACE,{"disambiguationData":[TD([[makeQuery(id+"F0.imprint","IMPRINT",EDGE,{"derivedFrom":subQ5}),1.0]])]});}
            var Q87;
            {var subQ5=sQuery(id+"F0.wireOp",EDGE,"E99");Q87=makeQuery(id+"F0.imprint","IMPRINT",FACE,{"disambiguationData":[TD([[makeQuery(id+"F0.imprint","IMPRINT",EDGE,{"derivedFrom":subQ5}),-1.0]])]});}
            var Q88;
            {var subQ5=sQuery(id+"F0.wireOp",EDGE,"y9LbIMTS-BwYh-9fh9-UmiA-ZNYAZaJqxmAJ");Q88=makeQuery(id+"F0.imprint","IMPRINT",FACE,{"disambiguationData":[TD([[makeQuery(id+"F0.imprint","IMPRINT",EDGE,{"derivedFrom":subQ5}),1.0]])]});}
            var Q89;
            Q89=makeQuery(id+"F0.imprint","IMPRINT",FACE,{"disambiguationData":[TD([[makeQuery(id+"F0.imprint","IMPRINT",EDGE,{"derivedFrom":sQuery(id+"F0.wireOp",EDGE,"y9LbIMTS-BwYh-9fh9-UmiA-ZNYAZaJqxmAJ")}),-1.0]])]});
            var Q90;
            {var subQ5=sQuery(id+"F0.wireOp",EDGE,"E100");Q90=makeQuery(id+"F0.imprint","IMPRINT",FACE,{"disambiguationData":[TD([[makeQuery(id+"F0.imprint","IMPRINT",EDGE,{"derivedFrom":subQ5}),1.0]])]});}
            var Q91;
            Q91=makeQuery(id+"F0.imprint","IMPRINT",FACE,{"disambiguationData":[TD([[makeQuery(id+"F0.imprint","IMPRINT",EDGE,{"derivedFrom":sQuery(id+"F0.wireOp",EDGE,"5feUKaIZ-YVe4-5bwL-nohM-rUMzkgmBEeui")}),1.0]])]});
            var Q92;
            {var subQ0=sQuery(id+"F0.wireOp",EDGE,"9VRpmUI2-KmG0-2DO5-QU92-hNNclBd8RN3t");Q92=makeQuery(id+"F0.imprint","IMPRINT",FACE,{"disambiguationData":[TD([[makeQuery(id+"F0.imprint","IMPRINT",EDGE,{"derivedFrom":subQ0}),1.0]])]});}
            var Q93;
            {var subQ0=sQuery(id+"F0.wireOp",EDGE,"5feUKaIZ-YVe4-5bwL-nohM-rUMzkgmBEeui");Q93=makeQuery(id+"F0.imprint","IMPRINT",FACE,{"disambiguationData":[TD([[makeQuery(id+"F0.imprint","IMPRINT",EDGE,{"derivedFrom":subQ0}),-1.0]])]});}
            var Q94;
            {var subQ2=sQuery(id+"F0.wireOp",EDGE,"E101");Q94=makeQuery(id+"F0.imprint","IMPRINT",FACE,{"disambiguationData":[TD([[makeQuery(id+"F0.imprint","IMPRINT",EDGE,{"derivedFrom":subQ2}),1.0]])]});}
            var Q95;
            {var subQ0=sQuery(id+"F0.wireOp",EDGE,"E5");var subQ3=sQuery(id+"F0.wireOp",EDGE,"E85.MirrorCS");var subQ5=makeQuery(id+"F0.imprint","INTERSECT",VERTEX,{"derivedFrom":[subQ0,subQ3]});Q95=makeQuery(id+"F0.imprint","IMPRINT",FACE,{"disambiguationData":[TD([[makeQuery(id+"F0.imprint","IMPRINT",EDGE,{"disambiguationData":[TD([[subQ5,-1.0]])],"derivedFrom":subQ3}),-1.0]])]});}
            var Q96;
            {var subQ11=sQuery(id+"F0.wireOp",EDGE,"E104");Q96=makeQuery(id+"F0.imprint","IMPRINT",FACE,{"disambiguationData":[TD([[makeQuery(id+"F0.imprint","IMPRINT",EDGE,{"derivedFrom":subQ11}),-1.0]])]});}
            var Q97;
            Q97=makeQuery(id+"F0.imprint","IMPRINT",FACE,{"disambiguationData":[TD([[makeQuery(id+"F0.imprint","IMPRINT",EDGE,{"derivedFrom":sQuery(id+"F0.wireOp",EDGE,"E100")}),-1.0]])]});
            var Q98;
            {var subQ0=sQuery(id+"F0.wireOp",EDGE,"E4");var subQ3=sQuery(id+"F0.wireOp",EDGE,"E73.MirrorCS");var subQ5=makeQuery(id+"F0.imprint","INTERSECT",VERTEX,{"derivedFrom":[subQ0,subQ3]});Q98=makeQuery(id+"F0.imprint","IMPRINT",FACE,{"disambiguationData":[TD([[makeQuery(id+"F0.imprint","IMPRINT",EDGE,{"disambiguationData":[TD([[subQ5,-1.0]])],"derivedFrom":subQ3}),1.0]])]});}
            extrude(context, id + "F1", {"entities" : qUnion([Q0, Q1, Q2, Q3, Q4, Q5, Q6, Q7, Q8, Q9, Q10, Q11, Q12, Q13, Q14, Q15, Q16, Q17, Q18, Q19, Q20, Q21, Q22, Q23, Q24, Q25, Q26, Q27, Q28, Q29, Q30, Q31, Q32, Q33, Q34, Q35, Q36, Q37, Q38, Q39, Q40, Q41, Q42, Q43, Q44, Q45, Q46, Q47, Q48, Q49, Q50, Q51, Q52, Q53, Q54, Q55, Q56, Q57, Q58, Q59, Q60, Q61, Q62, Q63, Q64, Q65, Q66, Q67, Q68, Q69, Q70, Q71, Q72, Q73, Q74, Q75, Q76, Q77, Q78, Q79, Q80, Q81, Q82, Q83, Q84, Q85, Q86, Q87, Q88, Q89, Q90, Q91, Q92, Q93, Q94, Q95, Q96, Q97, Q98]), "depth" : 4 * mm});
        }
        {
            var Q0;
            {var subQ0=sQuery(id+"F0.wireOp",EDGE,"E71.1.0.1");Q0=makeQuery(id+"F0.imprint","IMPRINT",FACE,{"disambiguationData":[TD([[makeQuery(id+"F0.imprint","IMPRINT",EDGE,{"derivedFrom":subQ0}),-1.0]])]});}
            var Q1;
            {var subQ0=sQuery(id+"F0.wireOp",EDGE,"E69");Q1=makeQuery(id+"F0.imprint","IMPRINT",FACE,{"disambiguationData":[TD([[makeQuery(id+"F0.imprint","IMPRINT",EDGE,{"derivedFrom":subQ0}),-1.0]])]});}
            var Q2;
            {var subQ0=sQuery(id+"F0.wireOp",EDGE,"E70.MirrorCS");Q2=makeQuery(id+"F0.imprint","IMPRINT",FACE,{"disambiguationData":[TD([[makeQuery(id+"F0.imprint","IMPRINT",EDGE,{"derivedFrom":subQ0}),1.0]])]});}
            var Q3;
            {var subQ0=sQuery(id+"F0.wireOp",EDGE,"E75.MirrorCS");Q3=makeQuery(id+"F0.imprint","IMPRINT",FACE,{"disambiguationData":[TD([[makeQuery(id+"F0.imprint","IMPRINT",EDGE,{"derivedFrom":subQ0}),1.0]])]});}
            var Q4;
            {var subQ0=sQuery(id+"F0.wireOp",EDGE,"E15.MirrorCS");Q4=makeQuery(id+"F0.imprint","IMPRINT",FACE,{"disambiguationData":[TD([[makeQuery(id+"F0.imprint","IMPRINT",EDGE,{"derivedFrom":subQ0}),1.0]])]});}
            var Q5;
            {var subQ0=sQuery(id+"F0.wireOp",EDGE,"E16.MirrorCS");Q5=makeQuery(id+"F0.imprint","IMPRINT",FACE,{"disambiguationData":[TD([[makeQuery(id+"F0.imprint","IMPRINT",EDGE,{"derivedFrom":subQ0}),1.0]])]});}
            var Q6;
            {var subQ0=sQuery(id+"F0.wireOp",EDGE,"E9.MirrorCS");Q6=makeQuery(id+"F0.imprint","IMPRINT",FACE,{"disambiguationData":[TD([[makeQuery(id+"F0.imprint","IMPRINT",EDGE,{"derivedFrom":subQ0}),1.0]])]});}
            var Q7;
            {var subQ0=sQuery(id+"F0.wireOp",EDGE,"E8");Q7=makeQuery(id+"F0.imprint","IMPRINT",FACE,{"disambiguationData":[TD([[makeQuery(id+"F0.imprint","IMPRINT",EDGE,{"derivedFrom":subQ0}),-1.0]])]});}
            var Q8;
            {var subQ0=sQuery(id+"F0.wireOp",EDGE,"E11.0.1.1");Q8=makeQuery(id+"F0.imprint","IMPRINT",FACE,{"disambiguationData":[TD([[makeQuery(id+"F0.imprint","IMPRINT",EDGE,{"derivedFrom":subQ0}),-1.0]])]});}
            var Q9;
            {var subQ0=sQuery(id+"F0.wireOp",EDGE,"E11.0.2.1");Q9=makeQuery(id+"F0.imprint","IMPRINT",FACE,{"disambiguationData":[TD([[makeQuery(id+"F0.imprint","IMPRINT",EDGE,{"derivedFrom":subQ0}),-1.0]])]});}
            var Q10;
            {var subQ3=sQuery(id+"F0.wireOp",EDGE,"E58.MirrorCS");Q10=makeQuery(id+"F0.imprint","IMPRINT",FACE,{"disambiguationData":[TD([[makeQuery(id+"F0.imprint","IMPRINT",EDGE,{"derivedFrom":subQ3}),1.0]])]});}
            var Q11;
            {var subQ0=sQuery(id+"F0.wireOp",EDGE,"E79.MirrorCS");Q11=makeQuery(id+"F0.imprint","IMPRINT",FACE,{"disambiguationData":[TD([[makeQuery(id+"F0.imprint","IMPRINT",EDGE,{"derivedFrom":subQ0}),1.0]])]});}
            var Q12;
            {var subQ0=sQuery(id+"F0.wireOp",EDGE,"E80.MirrorCS");Q12=makeQuery(id+"F0.imprint","IMPRINT",FACE,{"disambiguationData":[TD([[makeQuery(id+"F0.imprint","IMPRINT",EDGE,{"derivedFrom":subQ0}),1.0]])]});}
            var Q13;
            {var subQ0=sQuery(id+"F0.wireOp",EDGE,"E92.MirrorCS");Q13=makeQuery(id+"F0.imprint","IMPRINT",FACE,{"disambiguationData":[TD([[makeQuery(id+"F0.imprint","IMPRINT",EDGE,{"derivedFrom":subQ0}),-1.0]])]});}
            var Q14;
            {var subQ0=sQuery(id+"F0.wireOp",EDGE,"E88.MirrorCS");Q14=makeQuery(id+"F0.imprint","IMPRINT",FACE,{"disambiguationData":[TD([[makeQuery(id+"F0.imprint","IMPRINT",EDGE,{"derivedFrom":subQ0}),-1.0]])]});}
            var Q15;
            {var subQ0=sQuery(id+"F0.wireOp",EDGE,"E29.MirrorCS");Q15=makeQuery(id+"F0.imprint","IMPRINT",FACE,{"disambiguationData":[TD([[makeQuery(id+"F0.imprint","IMPRINT",EDGE,{"derivedFrom":subQ0}),1.0]])]});}
            var Q16;
            {var subQ0=sQuery(id+"F0.wireOp",EDGE,"E35.MirrorCS");Q16=makeQuery(id+"F0.imprint","IMPRINT",FACE,{"disambiguationData":[TD([[makeQuery(id+"F0.imprint","IMPRINT",EDGE,{"derivedFrom":subQ0}),-1.0]])]});}
            var Q17;
            {var subQ0=sQuery(id+"F0.wireOp",EDGE,"E26.MirrorCS");Q17=makeQuery(id+"F0.imprint","IMPRINT",FACE,{"disambiguationData":[TD([[makeQuery(id+"F0.imprint","IMPRINT",EDGE,{"derivedFrom":subQ0}),-1.0]])]});}
            var Q18;
            {var subQ0=sQuery(id+"F0.wireOp",EDGE,"E25.MirrorCS");Q18=makeQuery(id+"F0.imprint","IMPRINT",FACE,{"disambiguationData":[TD([[makeQuery(id+"F0.imprint","IMPRINT",EDGE,{"derivedFrom":subQ0}),1.0]])]});}
            var Q19;
            {var subQ0=sQuery(id+"F0.wireOp",EDGE,"E32.MirrorCS");Q19=makeQuery(id+"F0.imprint","IMPRINT",FACE,{"disambiguationData":[TD([[makeQuery(id+"F0.imprint","IMPRINT",EDGE,{"derivedFrom":subQ0}),-1.0]])]});}
            var Q20;
            {var subQ0=sQuery(id+"F0.wireOp",EDGE,"E27.MirrorCS");Q20=makeQuery(id+"F0.imprint","IMPRINT",FACE,{"disambiguationData":[TD([[makeQuery(id+"F0.imprint","IMPRINT",EDGE,{"derivedFrom":subQ0}),-1.0]])]});}
            var Q21;
            {var subQ3=sQuery(id+"F0.wireOp",EDGE,"E53.4.0.2");Q21=makeQuery(id+"F0.imprint","IMPRINT",FACE,{"disambiguationData":[TD([[makeQuery(id+"F0.imprint","IMPRINT",EDGE,{"derivedFrom":subQ3}),-1.0]])]});}
            var Q22;
            {var subQ0=sQuery(id+"F0.wireOp",EDGE,"E53.3.0.2");Q22=makeQuery(id+"F0.imprint","IMPRINT",FACE,{"disambiguationData":[TD([[makeQuery(id+"F0.imprint","IMPRINT",EDGE,{"derivedFrom":subQ0}),-1.0]])]});}
            var Q23;
            {var subQ0=sQuery(id+"F0.wireOp",EDGE,"E53.2.0.2");Q23=makeQuery(id+"F0.imprint","IMPRINT",FACE,{"disambiguationData":[TD([[makeQuery(id+"F0.imprint","IMPRINT",EDGE,{"derivedFrom":subQ0}),-1.0]])]});}
            var Q24;
            {var subQ0=sQuery(id+"F0.wireOp",EDGE,"E53.1.0.2");Q24=makeQuery(id+"F0.imprint","IMPRINT",FACE,{"disambiguationData":[TD([[makeQuery(id+"F0.imprint","IMPRINT",EDGE,{"derivedFrom":subQ0}),-1.0]])]});}
            var Q25;
            {var subQ0=sQuery(id+"F0.wireOp",EDGE,"E51");Q25=makeQuery(id+"F0.imprint","IMPRINT",FACE,{"disambiguationData":[TD([[makeQuery(id+"F0.imprint","IMPRINT",EDGE,{"derivedFrom":subQ0}),-1.0]])]});}
            var Q26;
            {var subQ0=sQuery(id+"F0.wireOp",EDGE,"E52.MirrorCS");Q26=makeQuery(id+"F0.imprint","IMPRINT",FACE,{"disambiguationData":[TD([[makeQuery(id+"F0.imprint","IMPRINT",EDGE,{"derivedFrom":subQ0}),1.0]])]});}
            var Q27;
            {var subQ0=sQuery(id+"F0.wireOp",EDGE,"E57.MirrorCS");Q27=makeQuery(id+"F0.imprint","IMPRINT",FACE,{"disambiguationData":[TD([[makeQuery(id+"F0.imprint","IMPRINT",EDGE,{"derivedFrom":subQ0}),1.0]])]});}
            var Q28;
            {var subQ0=sQuery(id+"F0.wireOp",EDGE,"E54.MirrorCS");Q28=makeQuery(id+"F0.imprint","IMPRINT",FACE,{"disambiguationData":[TD([[makeQuery(id+"F0.imprint","IMPRINT",EDGE,{"derivedFrom":subQ0}),1.0]])]});}
            var Q29;
            {var subQ0=sQuery(id+"F0.wireOp",EDGE,"E60.MirrorCS");Q29=makeQuery(id+"F0.imprint","IMPRINT",FACE,{"disambiguationData":[TD([[makeQuery(id+"F0.imprint","IMPRINT",EDGE,{"derivedFrom":subQ0}),-1.0]])]});}
            var Q30;
            {var subQ3=sQuery(id+"F0.wireOp",EDGE,"mMTmUIPN-TB5v-eayI-lI8k-IGmVwlv3VfPo");Q30=makeQuery(id+"F0.imprint","IMPRINT",FACE,{"disambiguationData":[TD([[makeQuery(id+"F0.imprint","IMPRINT",EDGE,{"derivedFrom":subQ3}),-1.0]])]});}
            extrude(context, id + "F2", {"entities" : qUnion([Q0, Q1, Q2, Q3, Q4, Q5, Q6, Q7, Q8, Q9, Q10, Q11, Q12, Q13, Q14, Q15, Q16, Q17, Q18, Q19, Q20, Q21, Q22, Q23, Q24, Q25, Q26, Q27, Q28, Q29, Q30]), "depth" : 4 * mm});
        }
        {
            var Q0;
            {var subQ0=sQuery(id+"F0.wireOp",EDGE,"E1.top");var subQ1=makeQuery(id+"F0.imprint","INTERSECT",VERTEX,{"derivedFrom":[subQ0,sQuery(id+"F0.wireOp",EDGE,"E48")]});Q0=makeQuery(id+"F1.opExtrude","SWEPT_FACE",FACE,{"disambiguationData":[OSD([subQ0]),TDD([makeQuery(id+"F0.imprint","IMPRINT",EDGE,{"disambiguationData":[TD([[subQ1,1.0]])],"derivedFrom":subQ0}),makeQuery(id+"F0.imprint","IMPRINT",EDGE,{"disambiguationData":[TD([[subQ1,-1.0]])],"derivedFrom":subQ0})])]});}
            var sketch = newSketch(context, id + "F3", { "sketchPlane" : qUnion([Q0])});
            skLineSegment(sketch, "E106.0.1", {"start": v(-85, 0) * mm, "end": v(-85, 4) * mm});
            skLineSegment(sketch, "E106.1.1", {"start": v(-75, 0) * mm, "end": v(-75, 4) * mm});
            skLineSegment(sketch, "E106.1.3", {"start": v(-85, 4) * mm, "end": v(-85, 0) * mm});
            skLineSegment(sketch, "E106.2.1", {"start": v(-65, 0) * mm, "end": v(-65, 4) * mm});
            skLineSegment(sketch, "E106.2.3", {"start": v(-75, 4) * mm, "end": v(-75, 0) * mm});
            skLineSegment(sketch, "E106.3.1", {"start": v(-55, 0) * mm, "end": v(-55, 4) * mm});
            skLineSegment(sketch, "E106.3.3", {"start": v(-65, 4) * mm, "end": v(-65, 0) * mm});
            skLineSegment(sketch, "E106.4.1", {"start": v(-45, 0) * mm, "end": v(-45, 4) * mm});
            skLineSegment(sketch, "E106.4.3", {"start": v(-55, 4) * mm, "end": v(-55, 0) * mm});
            skLineSegment(sketch, "E106.5.1", {"start": v(-35, 0) * mm, "end": v(-35, 4) * mm});
            skLineSegment(sketch, "E106.5.3", {"start": v(-45, 4) * mm, "end": v(-45, 0) * mm});
            skLineSegment(sketch, "E106.6.1", {"start": v(-25, 0) * mm, "end": v(-25, 4) * mm});
            skLineSegment(sketch, "E106.6.3", {"start": v(-35, 4) * mm, "end": v(-35, 0) * mm});
            skLineSegment(sketch, "E106.7.1", {"start": v(-15, 0) * mm, "end": v(-15, 4) * mm});
            skLineSegment(sketch, "E106.7.3", {"start": v(-25, 4) * mm, "end": v(-25, 0) * mm});
            skLineSegment(sketch, "E106.8.1", {"start": v(-5, 0) * mm, "end": v(-5, 4) * mm});
            skLineSegment(sketch, "E106.8.3", {"start": v(-15, 4) * mm, "end": v(-15, 0) * mm});
            skLineSegment(sketch, "E106.9.1", {"start": v(15, 0) * mm, "end": v(15, 4) * mm});
            skLineSegment(sketch, "E106.9.3", {"start": v(5, 4) * mm, "end": v(5, 0) * mm});
            skLineSegment(sketch, "E106.10.1", {"start": v(25, 0) * mm, "end": v(25, 4) * mm});
            skLineSegment(sketch, "E106.10.3", {"start": v(15, 4) * mm, "end": v(15, 0) * mm});
            skLineSegment(sketch, "E106.11.1", {"start": v(35, 0) * mm, "end": v(35, 4) * mm});
            skLineSegment(sketch, "E106.11.3", {"start": v(25, 4) * mm, "end": v(25, 0) * mm});
            skLineSegment(sketch, "E106.12.1", {"start": v(45, 0) * mm, "end": v(45, 4) * mm});
            skLineSegment(sketch, "E106.12.3", {"start": v(35, 4) * mm, "end": v(35, 0) * mm});
            skLineSegment(sketch, "E106.13.1", {"start": v(55, 0) * mm, "end": v(55, 4) * mm});
            skLineSegment(sketch, "E106.13.3", {"start": v(45, 4) * mm, "end": v(45, 0) * mm});
            skLineSegment(sketch, "E106.14.1", {"start": v(65, 0) * mm, "end": v(65, 4) * mm});
            skLineSegment(sketch, "E106.14.3", {"start": v(55, 4) * mm, "end": v(55, 0) * mm});
            skLineSegment(sketch, "E106.15.1", {"start": v(75, 0) * mm, "end": v(75, 4) * mm});
            skLineSegment(sketch, "E106.15.3", {"start": v(65, 4) * mm, "end": v(65, 0) * mm});
            skLineSegment(sketch, "E106.16.1", {"start": v(85, 0) * mm, "end": v(85, 4) * mm});
            skLineSegment(sketch, "E106.16.3", {"start": v(75, 4) * mm, "end": v(75, 0) * mm});
            skLineSegment(sketch, "E106.17.3", {"start": v(85, 4) * mm, "end": v(85, 0) * mm});
            skLineSegment(sketch, "E107", {"start": v(5, 0) * mm, "end": v(-5, 0) * mm});
            skLineSegment(sketch, "E108.bottom", {"start": v(-100, 0) * mm, "end": v(100, 0) * mm});
            skLineSegment(sketch, "E108.top", {"start": v(-100, 100) * mm, "end": v(100, 100) * mm});
            skLineSegment(sketch, "E108.left", {"start": v(-100, 0) * mm, "end": v(-100, 100) * mm});
            skLineSegment(sketch, "E108.right", {"start": v(100, 0) * mm, "end": v(100, 100) * mm});
            skLineSegment(sketch, "E109", {"start": v(-100, 4) * mm, "end": v(100, 4) * mm});
            skLineSegment(sketch, "E110", {"start": v(0, 100) * mm, "end": v(0, 0) * mm, "construction": true});
            skLineSegment(sketch, "E111", {"start": v(-100, 50) * mm, "end": v(-96, 50) * mm});
            skPoint(sketch, "E111.endSnap0", {"position": v(-100, 50) * mm});
            skLineSegment(sketch, "E112", {"start": v(-96, 0) * mm, "end": v(-96, 100) * mm});
            skLineSegment(sketch, "E113", {"start": v(-100, 45) * mm, "end": v(-96, 45) * mm});
            skLineSegment(sketch, "E114.MirrorCS", {"start": v(-100, 55) * mm, "end": v(-96, 55) * mm});
            skPoint(sketch, "E115.0.1.0", {"position": v(-100, 30) * mm});
            skLineSegment(sketch, "E115.0.1.1", {"start": v(-100, 25) * mm, "end": v(-96, 25) * mm});
            skLineSegment(sketch, "E115.0.1.2", {"start": v(-100, 30) * mm, "end": v(-96, 30) * mm});
            skLineSegment(sketch, "E115.0.1.3", {"start": v(-100, 35) * mm, "end": v(-96, 35) * mm});
            skPoint(sketch, "E115.0.2.0", {"position": v(-100, 10) * mm});
            skLineSegment(sketch, "E115.0.2.1", {"start": v(-100, 5) * mm, "end": v(-96, 5) * mm});
            skLineSegment(sketch, "E115.0.2.2", {"start": v(-100, 10) * mm, "end": v(-96, 10) * mm});
            skLineSegment(sketch, "E115.0.2.3", {"start": v(-100, 15) * mm, "end": v(-96, 15) * mm});
            skLineSegment(sketch, "E115.direction1", {"start": v(-100, 45) * mm, "end": v(-75, 45) * mm, "construction": true});
            skLineSegment(sketch, "E115.direction2", {"start": v(-100, 45) * mm, "end": v(-100, 25) * mm, "construction": true});
            skLineSegment(sketch, "E116.MirrorCS", {"start": v(-100, 70) * mm, "end": v(-96, 70) * mm});
            skLineSegment(sketch, "E117.MirrorCS", {"start": v(-100, 75) * mm, "end": v(-96, 75) * mm});
            skLineSegment(sketch, "E118.MirrorCS", {"start": v(-100, 65) * mm, "end": v(-96, 65) * mm});
            skLineSegment(sketch, "E119.MirrorCS", {"start": v(-100, 95) * mm, "end": v(-96, 95) * mm});
            skLineSegment(sketch, "E120.MirrorCS", {"start": v(-100, 90) * mm, "end": v(-96, 90) * mm});
            skPoint(sketch, "E121.MirrorP", {"position": v(-100, 70) * mm});
            skLineSegment(sketch, "E122.MirrorCS", {"start": v(-100, 85) * mm, "end": v(-96, 85) * mm});
            skPoint(sketch, "E123.MirrorP", {"position": v(-100, 90) * mm});
            skLineSegment(sketch, "E124.MirrorCS", {"start": v(100, 70) * mm, "end": v(96, 70) * mm});
            skLineSegment(sketch, "E125.MirrorCS", {"start": v(100, 45) * mm, "end": v(96, 45) * mm});
            skLineSegment(sketch, "E126.MirrorCS", {"start": v(100, 50) * mm, "end": v(96, 50) * mm});
            skLineSegment(sketch, "E127.MirrorCS", {"start": v(100, 10) * mm, "end": v(96, 10) * mm});
            skLineSegment(sketch, "E128.MirrorCS", {"start": v(100, 95) * mm, "end": v(96, 95) * mm});
            skPoint(sketch, "E129.MirrorP", {"position": v(100, 10) * mm});
            skLineSegment(sketch, "E130.MirrorCS", {"start": v(100, 90) * mm, "end": v(96, 90) * mm});
            skLineSegment(sketch, "E131.MirrorCS", {"start": v(100, 15) * mm, "end": v(96, 15) * mm});
            skLineSegment(sketch, "E132.MirrorCS", {"start": v(100, 55) * mm, "end": v(96, 55) * mm});
            skLineSegment(sketch, "E133.MirrorCS", {"start": v(100, 30) * mm, "end": v(96, 30) * mm});
            skLineSegment(sketch, "E134.MirrorCS", {"start": v(100, 5) * mm, "end": v(96, 5) * mm});
            skPoint(sketch, "E135.MirrorP", {"position": v(100, 70) * mm});
            skPoint(sketch, "E136.MirrorP", {"position": v(100, 30) * mm});
            skLineSegment(sketch, "E137.MirrorCS", {"start": v(100, 45) * mm, "end": v(100, 25) * mm, "construction": true});
            skLineSegment(sketch, "E138.MirrorCS", {"start": v(100, 75) * mm, "end": v(96, 75) * mm});
            skPoint(sketch, "E139.MirrorP", {"position": v(100, 50) * mm});
            skPoint(sketch, "E140.MirrorP", {"position": v(100, 90) * mm});
            skLineSegment(sketch, "E141.MirrorCS", {"start": v(100, 25) * mm, "end": v(96, 25) * mm});
            skLineSegment(sketch, "E142.MirrorCS", {"start": v(100, 65) * mm, "end": v(96, 65) * mm});
            skLineSegment(sketch, "E143.MirrorCS", {"start": v(100, 35) * mm, "end": v(96, 35) * mm});
            skLineSegment(sketch, "E144.MirrorCS", {"start": v(100, 85) * mm, "end": v(96, 85) * mm});
            skLineSegment(sketch, "E145.MirrorCS", {"start": v(96, 0) * mm, "end": v(96, 100) * mm});
            skLineSegment(sketch, "E146", {"start": v(-100, 50) * mm, "end": v(100, 50) * mm, "construction": true});
            skLineSegment(sketch, "E147.MirrorCS", {"start": v(15, 100) * mm, "end": v(15, 96) * mm});
            skLineSegment(sketch, "E148.MirrorCS", {"start": v(85, 100) * mm, "end": v(85, 96) * mm});
            skLineSegment(sketch, "E149.MirrorCS", {"start": v(-45, 100) * mm, "end": v(-45, 96) * mm});
            skLineSegment(sketch, "E150.MirrorCS", {"start": v(-85, 100) * mm, "end": v(-85, 96) * mm});
            skLineSegment(sketch, "E151.MirrorCS", {"start": v(-65, 100) * mm, "end": v(-65, 96) * mm});
            skLineSegment(sketch, "E152.MirrorCS", {"start": v(55, 96) * mm, "end": v(55, 100) * mm});
            skLineSegment(sketch, "E153.MirrorCS", {"start": v(45, 100) * mm, "end": v(45, 96) * mm});
            skLineSegment(sketch, "E154.MirrorCS", {"start": v(75, 96) * mm, "end": v(75, 100) * mm});
            skLineSegment(sketch, "E155.MirrorCS", {"start": v(-15, 96) * mm, "end": v(-15, 100) * mm});
            skLineSegment(sketch, "E156.MirrorCS", {"start": v(-35, 100) * mm, "end": v(-35, 96) * mm});
            skLineSegment(sketch, "E157.MirrorCS", {"start": v(25, 96) * mm, "end": v(25, 100) * mm});
            skLineSegment(sketch, "E158.MirrorCS", {"start": v(-55, 100) * mm, "end": v(-55, 96) * mm});
            skLineSegment(sketch, "E159.MirrorCS", {"start": v(-25, 96) * mm, "end": v(-25, 100) * mm});
            skLineSegment(sketch, "E160.MirrorCS", {"start": v(35, 100) * mm, "end": v(35, 96) * mm});
            skLineSegment(sketch, "E161.MirrorCS", {"start": v(5, 100) * mm, "end": v(-5, 100) * mm});
            skLineSegment(sketch, "E162.MirrorCS", {"start": v(-75, 100) * mm, "end": v(-75, 96) * mm});
            skLineSegment(sketch, "E163.MirrorCS", {"start": v(65, 96) * mm, "end": v(65, 100) * mm});
            skLineSegment(sketch, "E164.MirrorCS", {"start": v(-25, 100) * mm, "end": v(-25, 96) * mm});
            skLineSegment(sketch, "E165.MirrorCS", {"start": v(35, 96) * mm, "end": v(35, 100) * mm});
            skLineSegment(sketch, "E166.MirrorCS", {"start": v(-5, 100) * mm, "end": v(-5, 96) * mm});
            skLineSegment(sketch, "E167.MirrorCS", {"start": v(45, 96) * mm, "end": v(45, 100) * mm});
            skLineSegment(sketch, "E168.MirrorCS", {"start": v(-85, 96) * mm, "end": v(-85, 100) * mm});
            skLineSegment(sketch, "E169.MirrorCS", {"start": v(-75, 96) * mm, "end": v(-75, 100) * mm});
            skLineSegment(sketch, "E170.MirrorCS", {"start": v(85, 96) * mm, "end": v(85, 100) * mm});
            skLineSegment(sketch, "E171.MirrorCS", {"start": v(65, 100) * mm, "end": v(65, 96) * mm});
            skLineSegment(sketch, "E172.MirrorCS", {"start": v(75, 100) * mm, "end": v(75, 96) * mm});
            skLineSegment(sketch, "E173.MirrorCS", {"start": v(15, 96) * mm, "end": v(15, 100) * mm});
            skLineSegment(sketch, "E174.MirrorCS", {"start": v(-35, 96) * mm, "end": v(-35, 100) * mm});
            skLineSegment(sketch, "E175.MirrorCS", {"start": v(55, 100) * mm, "end": v(55, 96) * mm});
            skLineSegment(sketch, "E176.MirrorCS", {"start": v(-15, 100) * mm, "end": v(-15, 96) * mm});
            skLineSegment(sketch, "E177.MirrorCS", {"start": v(25, 100) * mm, "end": v(25, 96) * mm});
            skLineSegment(sketch, "E178.MirrorCS", {"start": v(-100, 96) * mm, "end": v(100, 96) * mm});
            skLineSegment(sketch, "E179.MirrorCS", {"start": v(-65, 96) * mm, "end": v(-65, 100) * mm});
            skLineSegment(sketch, "E180.MirrorCS", {"start": v(-55, 96) * mm, "end": v(-55, 100) * mm});
            skLineSegment(sketch, "E181.MirrorCS", {"start": v(5, 96) * mm, "end": v(5, 100) * mm});
            skLineSegment(sketch, "E182.MirrorCS", {"start": v(-45, 96) * mm, "end": v(-45, 100) * mm});
            skSolve(sketch);
        }
        {
            var Q0;
            {var subQ4=sQuery(id+"F3.wireOp",EDGE,"E112");var subQ5=sQuery(id+"F3.wireOp",EDGE,"E108.top");var subQ6=makeQuery(id+"F3.imprint","INTERSECT",VERTEX,{"derivedFrom":[subQ5,subQ4]});Q0=makeQuery(id+"F3.imprint","IMPRINT",FACE,{"disambiguationData":[TD([[makeQuery(id+"F3.imprint","IMPRINT",EDGE,{"disambiguationData":[TD([[subQ6,-1.0]])],"derivedFrom":subQ5}),-1.0]])]});}
            var Q1;
            {var subQ0=sQuery(id+"F3.wireOp",EDGE,"E128.MirrorCS");Q1=makeQuery(id+"F3.imprint","IMPRINT",FACE,{"disambiguationData":[TD([[makeQuery(id+"F3.imprint","IMPRINT",EDGE,{"derivedFrom":subQ0}),1.0]])]});}
            var Q2;
            {var subQ0=sQuery(id+"F3.wireOp",EDGE,"E130.MirrorCS");Q2=makeQuery(id+"F3.imprint","IMPRINT",FACE,{"disambiguationData":[TD([[makeQuery(id+"F3.imprint","IMPRINT",EDGE,{"derivedFrom":subQ0}),1.0]])]});}
            var Q3;
            {var subQ0=sQuery(id+"F3.wireOp",EDGE,"E124.MirrorCS");Q3=makeQuery(id+"F3.imprint","IMPRINT",FACE,{"disambiguationData":[TD([[makeQuery(id+"F3.imprint","IMPRINT",EDGE,{"derivedFrom":subQ0}),-1.0]])]});}
            var Q4;
            {var subQ0=sQuery(id+"F3.wireOp",EDGE,"E124.MirrorCS");Q4=makeQuery(id+"F3.imprint","IMPRINT",FACE,{"disambiguationData":[TD([[makeQuery(id+"F3.imprint","IMPRINT",EDGE,{"derivedFrom":subQ0}),1.0]])]});}
            var Q5;
            {var subQ0=sQuery(id+"F3.wireOp",EDGE,"E126.MirrorCS");Q5=makeQuery(id+"F3.imprint","IMPRINT",FACE,{"disambiguationData":[TD([[makeQuery(id+"F3.imprint","IMPRINT",EDGE,{"derivedFrom":subQ0}),-1.0]])]});}
            var Q6;
            {var subQ0=sQuery(id+"F3.wireOp",EDGE,"E125.MirrorCS");Q6=makeQuery(id+"F3.imprint","IMPRINT",FACE,{"disambiguationData":[TD([[makeQuery(id+"F3.imprint","IMPRINT",EDGE,{"derivedFrom":subQ0}),-1.0]])]});}
            var Q7;
            {var subQ0=sQuery(id+"F3.wireOp",EDGE,"E133.MirrorCS");Q7=makeQuery(id+"F3.imprint","IMPRINT",FACE,{"disambiguationData":[TD([[makeQuery(id+"F3.imprint","IMPRINT",EDGE,{"derivedFrom":subQ0}),-1.0]])]});}
            var Q8;
            {var subQ0=sQuery(id+"F3.wireOp",EDGE,"E133.MirrorCS");Q8=makeQuery(id+"F3.imprint","IMPRINT",FACE,{"disambiguationData":[TD([[makeQuery(id+"F3.imprint","IMPRINT",EDGE,{"derivedFrom":subQ0}),1.0]])]});}
            var Q9;
            {var subQ0=sQuery(id+"F3.wireOp",EDGE,"E127.MirrorCS");Q9=makeQuery(id+"F3.imprint","IMPRINT",FACE,{"disambiguationData":[TD([[makeQuery(id+"F3.imprint","IMPRINT",EDGE,{"derivedFrom":subQ0}),-1.0]])]});}
            var Q10;
            {var subQ0=sQuery(id+"F3.wireOp",EDGE,"E127.MirrorCS");Q10=makeQuery(id+"F3.imprint","IMPRINT",FACE,{"disambiguationData":[TD([[makeQuery(id+"F3.imprint","IMPRINT",EDGE,{"derivedFrom":subQ0}),1.0]])]});}
            var Q11;
            {var subQ3=sQuery(id+"F3.wireOp",EDGE,"E134.MirrorCS");Q11=makeQuery(id+"F3.imprint","IMPRINT",FACE,{"disambiguationData":[TD([[makeQuery(id+"F3.imprint","IMPRINT",EDGE,{"derivedFrom":subQ3}),1.0]])]});}
            var Q12;
            {var subQ3=sQuery(id+"F3.wireOp",EDGE,"E115.0.2.1");Q12=makeQuery(id+"F3.imprint","IMPRINT",FACE,{"disambiguationData":[TD([[makeQuery(id+"F3.imprint","IMPRINT",EDGE,{"derivedFrom":subQ3}),-1.0]])]});}
            var Q13;
            {var subQ0=sQuery(id+"F3.wireOp",EDGE,"E115.0.2.1");Q13=makeQuery(id+"F3.imprint","IMPRINT",FACE,{"disambiguationData":[TD([[makeQuery(id+"F3.imprint","IMPRINT",EDGE,{"derivedFrom":subQ0}),1.0]])]});}
            var Q14;
            {var subQ0=sQuery(id+"F3.wireOp",EDGE,"E115.0.2.2");Q14=makeQuery(id+"F3.imprint","IMPRINT",FACE,{"disambiguationData":[TD([[makeQuery(id+"F3.imprint","IMPRINT",EDGE,{"derivedFrom":subQ0}),1.0]])]});}
            var Q15;
            {var subQ0=sQuery(id+"F3.wireOp",EDGE,"E115.0.1.1");Q15=makeQuery(id+"F3.imprint","IMPRINT",FACE,{"disambiguationData":[TD([[makeQuery(id+"F3.imprint","IMPRINT",EDGE,{"derivedFrom":subQ0}),1.0]])]});}
            var Q16;
            {var subQ0=sQuery(id+"F3.wireOp",EDGE,"E115.0.1.2");Q16=makeQuery(id+"F3.imprint","IMPRINT",FACE,{"disambiguationData":[TD([[makeQuery(id+"F3.imprint","IMPRINT",EDGE,{"derivedFrom":subQ0}),1.0]])]});}
            var Q17;
            {var subQ0=sQuery(id+"F3.wireOp",EDGE,"E111");Q17=makeQuery(id+"F3.imprint","IMPRINT",FACE,{"disambiguationData":[TD([[makeQuery(id+"F3.imprint","IMPRINT",EDGE,{"derivedFrom":subQ0}),-1.0]])]});}
            var Q18;
            {var subQ0=sQuery(id+"F3.wireOp",EDGE,"E111");Q18=makeQuery(id+"F3.imprint","IMPRINT",FACE,{"disambiguationData":[TD([[makeQuery(id+"F3.imprint","IMPRINT",EDGE,{"derivedFrom":subQ0}),1.0]])]});}
            var Q19;
            {var subQ0=sQuery(id+"F3.wireOp",EDGE,"E116.MirrorCS");Q19=makeQuery(id+"F3.imprint","IMPRINT",FACE,{"disambiguationData":[TD([[makeQuery(id+"F3.imprint","IMPRINT",EDGE,{"derivedFrom":subQ0}),1.0]])]});}
            var Q20;
            {var subQ0=sQuery(id+"F3.wireOp",EDGE,"E116.MirrorCS");Q20=makeQuery(id+"F3.imprint","IMPRINT",FACE,{"disambiguationData":[TD([[makeQuery(id+"F3.imprint","IMPRINT",EDGE,{"derivedFrom":subQ0}),-1.0]])]});}
            var Q21;
            {var subQ0=sQuery(id+"F3.wireOp",EDGE,"E120.MirrorCS");Q21=makeQuery(id+"F3.imprint","IMPRINT",FACE,{"disambiguationData":[TD([[makeQuery(id+"F3.imprint","IMPRINT",EDGE,{"derivedFrom":subQ0}),-1.0]])]});}
            var Q22;
            {var subQ0=sQuery(id+"F3.wireOp",EDGE,"E119.MirrorCS");Q22=makeQuery(id+"F3.imprint","IMPRINT",FACE,{"disambiguationData":[TD([[makeQuery(id+"F3.imprint","IMPRINT",EDGE,{"derivedFrom":subQ0}),-1.0]])]});}
            var Q23;
            {var subQ2=sQuery(id+"F3.wireOp",EDGE,"E109");var subQ42=makeQuery(id+"F3.imprint","INTERSECT",VERTEX,{"derivedFrom":[sQuery(id+"F3.wireOp",EDGE,"E106.1.3"),subQ2]});Q23=makeQuery(id+"F3.imprint","IMPRINT",FACE,{"disambiguationData":[TD([[makeQuery(id+"F3.imprint","IMPRINT",EDGE,{"disambiguationData":[TD([[subQ42,1.0]])],"derivedFrom":subQ2}),1.0]])]});}
            var Q24;
            {var subQ0=sQuery(id+"F3.wireOp",EDGE,"E171.MirrorCS");Q24=makeQuery(id+"F3.imprint","IMPRINT",FACE,{"disambiguationData":[TD([[makeQuery(id+"F3.imprint","IMPRINT",EDGE,{"derivedFrom":subQ0}),1.0]])]});}
            var Q25;
            {var subQ0=sQuery(id+"F3.wireOp",EDGE,"E167.MirrorCS");Q25=makeQuery(id+"F3.imprint","IMPRINT",FACE,{"disambiguationData":[TD([[makeQuery(id+"F3.imprint","IMPRINT",EDGE,{"derivedFrom":subQ0}),-1.0]])]});}
            var Q26;
            {var subQ0=sQuery(id+"F3.wireOp",EDGE,"E165.MirrorCS");Q26=makeQuery(id+"F3.imprint","IMPRINT",FACE,{"disambiguationData":[TD([[makeQuery(id+"F3.imprint","IMPRINT",EDGE,{"derivedFrom":subQ0}),1.0]])]});}
            var Q27;
            {var subQ0=sQuery(id+"F3.wireOp",EDGE,"E173.MirrorCS");Q27=makeQuery(id+"F3.imprint","IMPRINT",FACE,{"disambiguationData":[TD([[makeQuery(id+"F3.imprint","IMPRINT",EDGE,{"derivedFrom":subQ0}),1.0]])]});}
            var Q28;
            {var subQ0=sQuery(id+"F3.wireOp",EDGE,"E166.MirrorCS");Q28=makeQuery(id+"F3.imprint","IMPRINT",FACE,{"disambiguationData":[TD([[makeQuery(id+"F3.imprint","IMPRINT",EDGE,{"derivedFrom":subQ0}),-1.0]])]});}
            var Q29;
            {var subQ0=sQuery(id+"F3.wireOp",EDGE,"E164.MirrorCS");Q29=makeQuery(id+"F3.imprint","IMPRINT",FACE,{"disambiguationData":[TD([[makeQuery(id+"F3.imprint","IMPRINT",EDGE,{"derivedFrom":subQ0}),-1.0]])]});}
            var Q30;
            {var subQ0=sQuery(id+"F3.wireOp",EDGE,"E180.MirrorCS");Q30=makeQuery(id+"F3.imprint","IMPRINT",FACE,{"disambiguationData":[TD([[makeQuery(id+"F3.imprint","IMPRINT",EDGE,{"derivedFrom":subQ0}),-1.0]])]});}
            var Q31;
            {var subQ0=sQuery(id+"F3.wireOp",EDGE,"E169.MirrorCS");Q31=makeQuery(id+"F3.imprint","IMPRINT",FACE,{"disambiguationData":[TD([[makeQuery(id+"F3.imprint","IMPRINT",EDGE,{"derivedFrom":subQ0}),-1.0]])]});}
            var Q32;
            {var subQ5=sQuery(id+"F3.wireOp",EDGE,"E168.MirrorCS");Q32=makeQuery(id+"F3.imprint","IMPRINT",FACE,{"disambiguationData":[TD([[makeQuery(id+"F3.imprint","IMPRINT",EDGE,{"derivedFrom":subQ5}),1.0]])]});}
            var Q33;
            {var subQ0=sQuery(id+"F3.wireOp",EDGE,"E119.MirrorCS");Q33=makeQuery(id+"F3.imprint","IMPRINT",FACE,{"disambiguationData":[TD([[makeQuery(id+"F3.imprint","IMPRINT",EDGE,{"derivedFrom":subQ0}),1.0]])]});}
            var Q34;
            {var subQ5=sQuery(id+"F3.wireOp",EDGE,"E170.MirrorCS");Q34=makeQuery(id+"F3.imprint","IMPRINT",FACE,{"disambiguationData":[TD([[makeQuery(id+"F3.imprint","IMPRINT",EDGE,{"derivedFrom":subQ5}),-1.0]])]});}
            var Q35;
            {var subQ3=sQuery(id+"F3.wireOp",EDGE,"E128.MirrorCS");Q35=makeQuery(id+"F3.imprint","IMPRINT",FACE,{"disambiguationData":[TD([[makeQuery(id+"F3.imprint","IMPRINT",EDGE,{"derivedFrom":subQ3}),-1.0]])]});}
            var Q36;
            {var subQ0=sQuery(id+"F3.wireOp",EDGE,"E130.MirrorCS");Q36=makeQuery(id+"F3.imprint","IMPRINT",FACE,{"disambiguationData":[TD([[makeQuery(id+"F3.imprint","IMPRINT",EDGE,{"derivedFrom":subQ0}),-1.0]])]});}
            extrude(context, id + "F4", {"entities" : qUnion([Q0, Q1, Q2, Q3, Q4, Q5, Q6, Q7, Q8, Q9, Q10, Q11, Q12, Q13, Q14, Q15, Q16, Q17, Q18, Q19, Q20, Q21, Q22, Q23, Q24, Q25, Q26, Q27, Q28, Q29, Q30, Q31, Q32, Q33, Q34, Q35, Q36]), "oppositeDirection" : true, "depth" : 4 * mm});
        }
        {
            var Q0;
            Q0=makeQuery(id+"F4.opExtrude","SWEPT_BODY",BODY,{"disambiguationData":[OSD([sQuery(id+"F3.wireOp",EDGE,"E108.top"),sQuery(id+"F3.wireOp",EDGE,"E108.left"),sQuery(id+"F3.wireOp",EDGE,"E108.right"),sQuery(id+"F3.wireOp",EDGE,"E109")])]});
            var Q1;
            Q1=makeQuery(id+"F2.opExtrude","SWEPT_BODY",BODY,{"disambiguationData":[OSD([sQuery(id+"F0.wireOp",EDGE,"E1.top"),sQuery(id+"F0.wireOp",EDGE,"E1.left"),sQuery(id+"F0.wireOp",EDGE,"E7"),sQuery(id+"F0.wireOp",EDGE,"E11.0.3.1"),sQuery(id+"F0.wireOp",EDGE,"E49"),sQuery(id+"F0.wireOp",EDGE,"E58.MirrorCS")])]});
            var Q2;
            Q2=makeQuery(id+"F2.opExtrude","SWEPT_BODY",BODY,{"disambiguationData":[OSD([sQuery(id+"F0.wireOp",EDGE,"E1.top"),sQuery(id+"F0.wireOp",EDGE,"E49"),sQuery(id+"F0.wireOp",EDGE,"E60.MirrorCS"),sQuery(id+"F0.wireOp",EDGE,"E62.MirrorCS")])]});
            var Q3;
            Q3=makeQuery(id+"F2.opExtrude","SWEPT_BODY",BODY,{"disambiguationData":[OSD([sQuery(id+"F0.wireOp",EDGE,"E1.top"),sQuery(id+"F0.wireOp",EDGE,"E49"),sQuery(id+"F0.wireOp",EDGE,"E54.MirrorCS"),sQuery(id+"F0.wireOp",EDGE,"E56.MirrorCS")])]});
            var Q4;
            Q4=makeQuery(id+"F2.opExtrude","SWEPT_BODY",BODY,{"disambiguationData":[OSD([sQuery(id+"F0.wireOp",EDGE,"E1.top"),sQuery(id+"F0.wireOp",EDGE,"E49"),sQuery(id+"F0.wireOp",EDGE,"E57.MirrorCS"),sQuery(id+"F0.wireOp",EDGE,"E65.MirrorCS")])]});
            var Q5;
            Q5=makeQuery(id+"F2.opExtrude","SWEPT_BODY",BODY,{"disambiguationData":[OSD([sQuery(id+"F0.wireOp",EDGE,"E1.top"),sQuery(id+"F0.wireOp",EDGE,"E49"),sQuery(id+"F0.wireOp",EDGE,"E52.MirrorCS"),sQuery(id+"F0.wireOp",EDGE,"E61.MirrorCS")])]});
            var Q6;
            Q6=makeQuery(id+"F2.opExtrude","SWEPT_BODY",BODY,{"disambiguationData":[OSD([sQuery(id+"F0.wireOp",EDGE,"E1.top"),sQuery(id+"F0.wireOp",EDGE,"E50.MirrorCS"),sQuery(id+"F0.wireOp",EDGE,"E51"),sQuery(id+"F0.wireOp",EDGE,"E53.1.0.0")])]});
            var Q7;
            Q7=makeQuery(id+"F2.opExtrude","SWEPT_BODY",BODY,{"disambiguationData":[OSD([sQuery(id+"F0.wireOp",EDGE,"E1.top"),sQuery(id+"F0.wireOp",EDGE,"E50.MirrorCS"),sQuery(id+"F0.wireOp",EDGE,"E53.1.0.2"),sQuery(id+"F0.wireOp",EDGE,"E53.2.0.0")])]});
            var Q8;
            Q8=makeQuery(id+"F2.opExtrude","SWEPT_BODY",BODY,{"disambiguationData":[OSD([sQuery(id+"F0.wireOp",EDGE,"E1.top"),sQuery(id+"F0.wireOp",EDGE,"E50.MirrorCS"),sQuery(id+"F0.wireOp",EDGE,"E53.2.0.2"),sQuery(id+"F0.wireOp",EDGE,"E53.3.0.0")])]});
            var Q9;
            Q9=makeQuery(id+"F2.opExtrude","SWEPT_BODY",BODY,{"disambiguationData":[OSD([sQuery(id+"F0.wireOp",EDGE,"E1.top"),sQuery(id+"F0.wireOp",EDGE,"E50.MirrorCS"),sQuery(id+"F0.wireOp",EDGE,"E53.3.0.2"),sQuery(id+"F0.wireOp",EDGE,"E53.4.0.0")])]});
            var Q10;
            Q10=makeQuery(id+"F2.opExtrude","SWEPT_BODY",BODY,{"disambiguationData":[OSD([sQuery(id+"F0.wireOp",EDGE,"E1.top"),sQuery(id+"F0.wireOp",EDGE,"E1.right"),sQuery(id+"F0.wireOp",EDGE,"E23.MirrorCS"),sQuery(id+"F0.wireOp",EDGE,"E31.MirrorCS"),sQuery(id+"F0.wireOp",EDGE,"E50.MirrorCS"),sQuery(id+"F0.wireOp",EDGE,"E53.4.0.2")])]});
            booleanBodies(context, id + "F5", {"operationType" : BooleanOperationType.UNION, "tools" : qUnion([Q0, Q1, Q2, Q3, Q4, Q5, Q6, Q7, Q8, Q9, Q10])});
        }
        {
            var Q0;
            {var subQ5=sQuery(id+"F3.wireOp",EDGE,"E128.MirrorCS");Q0=makeQuery(id+"F3.imprint","IMPRINT",FACE,{"disambiguationData":[TD([[makeQuery(id+"F3.imprint","IMPRINT",EDGE,{"derivedFrom":subQ5}),-1.0]])]});}
            var Q1;
            {var subQ0=sQuery(id+"F3.wireOp",EDGE,"E138.MirrorCS");Q1=makeQuery(id+"F3.imprint","IMPRINT",FACE,{"disambiguationData":[TD([[makeQuery(id+"F3.imprint","IMPRINT",EDGE,{"derivedFrom":subQ0}),-1.0]])]});}
            var Q2;
            {var subQ0=sQuery(id+"F3.wireOp",EDGE,"E132.MirrorCS");Q2=makeQuery(id+"F3.imprint","IMPRINT",FACE,{"disambiguationData":[TD([[makeQuery(id+"F3.imprint","IMPRINT",EDGE,{"derivedFrom":subQ0}),-1.0]])]});}
            var Q3;
            {var subQ0=sQuery(id+"F3.wireOp",EDGE,"E125.MirrorCS");Q3=makeQuery(id+"F3.imprint","IMPRINT",FACE,{"disambiguationData":[TD([[makeQuery(id+"F3.imprint","IMPRINT",EDGE,{"derivedFrom":subQ0}),1.0]])]});}
            var Q4;
            {var subQ0=sQuery(id+"F3.wireOp",EDGE,"E131.MirrorCS");Q4=makeQuery(id+"F3.imprint","IMPRINT",FACE,{"disambiguationData":[TD([[makeQuery(id+"F3.imprint","IMPRINT",EDGE,{"derivedFrom":subQ0}),-1.0]])]});}
            var Q5;
            {var subQ0=sQuery(id+"F3.wireOp",EDGE,"E114.MirrorCS");Q5=makeQuery(id+"F3.imprint","IMPRINT",FACE,{"disambiguationData":[TD([[makeQuery(id+"F3.imprint","IMPRINT",EDGE,{"derivedFrom":subQ0}),1.0]])]});}
            var Q6;
            {var subQ0=sQuery(id+"F3.wireOp",EDGE,"E113");Q6=makeQuery(id+"F3.imprint","IMPRINT",FACE,{"disambiguationData":[TD([[makeQuery(id+"F3.imprint","IMPRINT",EDGE,{"derivedFrom":subQ0}),-1.0]])]});}
            var Q7;
            {var subQ0=sQuery(id+"F3.wireOp",EDGE,"E115.0.1.1");Q7=makeQuery(id+"F3.imprint","IMPRINT",FACE,{"disambiguationData":[TD([[makeQuery(id+"F3.imprint","IMPRINT",EDGE,{"derivedFrom":subQ0}),-1.0]])]});}
            var Q8;
            {var subQ0=sQuery(id+"F3.wireOp",EDGE,"E117.MirrorCS");Q8=makeQuery(id+"F3.imprint","IMPRINT",FACE,{"disambiguationData":[TD([[makeQuery(id+"F3.imprint","IMPRINT",EDGE,{"derivedFrom":subQ0}),1.0]])]});}
            extrude(context, id + "F6", {"entities" : qUnion([Q0, Q1, Q2, Q3, Q4, Q5, Q6, Q7, Q8]), "oppositeDirection" : true, "depth" : 4 * mm});
        }
        {
            var Q0;
            {var subQ0=sQuery(id+"F0.wireOp",EDGE,"E1.right");Q0=makeQuery(id+"F1.opExtrude","SWEPT_FACE",FACE,{"disambiguationData":[OSD([subQ0]),TDD([makeQuery(id+"F0.imprint","IMPRINT",EDGE,{"disambiguationData":[TD([[makeQuery(id+"F0.imprint","INTERSECT",VERTEX,{"derivedFrom":[subQ0,sQuery(id+"F0.wireOp",EDGE,"E26.MirrorCS")]}),-1.0]])],"derivedFrom":subQ0}),makeQuery(id+"F0.imprint","IMPRINT",EDGE,{"disambiguationData":[TD([[makeQuery(id+"F0.imprint","INTERSECT",VERTEX,{"derivedFrom":[subQ0,sQuery(id+"F0.wireOp",EDGE,"E25.MirrorCS")]}),1.0]])],"derivedFrom":subQ0})])]});}
            var sketch = newSketch(context, id + "F7", { "sketchPlane" : qUnion([Q0])});
            skLineSegment(sketch, "E183.bottom", {"start": v(-100, 100) * mm, "end": v(50, 100) * mm});
            skLineSegment(sketch, "E183.top", {"start": v(-100, 0) * mm, "end": v(50, 0) * mm});
            skLineSegment(sketch, "E183.left", {"start": v(-100, 100) * mm, "end": v(-100, 0) * mm});
            skLineSegment(sketch, "E183.right", {"start": v(50, 100) * mm, "end": v(50, 0) * mm});
            skLineSegment(sketch, "E184", {"start": v(-100, 4) * mm, "end": v(50, 4) * mm});
            skLineSegment(sketch, "E185", {"start": v(-96, 100) * mm, "end": v(-96, 4) * mm});
            skLineSegment(sketch, "E186", {"start": v(50, 50) * mm, "end": v(46, 50) * mm});
            skLineSegment(sketch, "E187", {"start": v(46, 0) * mm, "end": v(46, 100) * mm});
            skLineSegment(sketch, "E188", {"start": v(50, 55) * mm, "end": v(46, 55) * mm});
            skLineSegment(sketch, "E189.MirrorCS", {"start": v(50, 45) * mm, "end": v(46, 45) * mm});
            skLineSegment(sketch, "E190.0.1.0", {"start": v(50, 65) * mm, "end": v(46, 65) * mm});
            skLineSegment(sketch, "E190.0.1.1", {"start": v(50, 70) * mm, "end": v(46, 70) * mm});
            skLineSegment(sketch, "E190.0.1.2", {"start": v(50, 75) * mm, "end": v(46, 75) * mm});
            skLineSegment(sketch, "E190.0.2.0", {"start": v(50, 85) * mm, "end": v(46, 85) * mm});
            skLineSegment(sketch, "E190.0.2.1", {"start": v(50, 90) * mm, "end": v(46, 90) * mm});
            skLineSegment(sketch, "E190.0.2.2", {"start": v(50, 95) * mm, "end": v(46, 95) * mm});
            skLineSegment(sketch, "E190.direction1", {"start": v(46, 45) * mm, "end": v(71, 45) * mm, "construction": true});
            skLineSegment(sketch, "E190.direction2", {"start": v(46, 45) * mm, "end": v(46, 65) * mm, "construction": true});
            skLineSegment(sketch, "E191.MirrorCS", {"start": v(50, 25) * mm, "end": v(46, 25) * mm});
            skLineSegment(sketch, "E192.MirrorCS", {"start": v(50, 30) * mm, "end": v(46, 30) * mm});
            skLineSegment(sketch, "E193.MirrorCS", {"start": v(50, 35) * mm, "end": v(46, 35) * mm});
            skLineSegment(sketch, "E194.MirrorCS", {"start": v(50, 5) * mm, "end": v(46, 5) * mm});
            skLineSegment(sketch, "E195.MirrorCS", {"start": v(50, 10) * mm, "end": v(46, 10) * mm});
            skLineSegment(sketch, "E196.MirrorCS", {"start": v(50, 15) * mm, "end": v(46, 15) * mm});
            skLineSegment(sketch, "E197", {"start": v(-100, 50) * mm, "end": v(50, 50) * mm, "construction": true});
            skLineSegment(sketch, "E198.1", {"start": v(-80, 4) * mm, "end": v(-80, 0) * mm});
            skLineSegment(sketch, "E198.4", {"start": v(-70, 4) * mm, "end": v(-70, 0) * mm});
            skLineSegment(sketch, "E198.5", {"start": v(-60, 4) * mm, "end": v(-60, 0) * mm});
            skLineSegment(sketch, "E198.6", {"start": v(-50, 4) * mm, "end": v(-50, 0) * mm});
            skLineSegment(sketch, "E198.7", {"start": v(-40, 4) * mm, "end": v(-40, 0) * mm});
            skLineSegment(sketch, "E198.8", {"start": v(-30, 4) * mm, "end": v(-30, 0) * mm});
            skLineSegment(sketch, "E198.9", {"start": v(-20, 4) * mm, "end": v(-20, 0) * mm});
            skLineSegment(sketch, "E198.10", {"start": v(-10, 4) * mm, "end": v(-10, 0) * mm});
            skLineSegment(sketch, "E198.11", {"start": v(0, 4) * mm, "end": v(0, 0) * mm});
            skLineSegment(sketch, "E198.12", {"start": v(10, 4) * mm, "end": v(10, 0) * mm});
            skLineSegment(sketch, "E198.13", {"start": v(20, 4) * mm, "end": v(20, 0) * mm});
            skLineSegment(sketch, "E198.14", {"start": v(30, 4) * mm, "end": v(30, 0) * mm});
            skLineSegment(sketch, "E199.MirrorCS", {"start": v(-60, 96) * mm, "end": v(-60, 100) * mm});
            skLineSegment(sketch, "E200.MirrorCS", {"start": v(-30, 96) * mm, "end": v(-30, 100) * mm});
            skLineSegment(sketch, "E201.MirrorCS", {"start": v(-10, 96) * mm, "end": v(-10, 100) * mm});
            skLineSegment(sketch, "E202.MirrorCS", {"start": v(10, 96) * mm, "end": v(10, 100) * mm});
            skLineSegment(sketch, "E203.MirrorCS", {"start": v(0, 96) * mm, "end": v(0, 100) * mm});
            skLineSegment(sketch, "E204.MirrorCS", {"start": v(-50, 96) * mm, "end": v(-50, 100) * mm});
            skLineSegment(sketch, "E205.MirrorCS", {"start": v(20, 96) * mm, "end": v(20, 100) * mm});
            skLineSegment(sketch, "E206.MirrorCS", {"start": v(-80, 96) * mm, "end": v(-80, 100) * mm});
            skLineSegment(sketch, "E207.MirrorCS", {"start": v(-40, 96) * mm, "end": v(-40, 100) * mm});
            skLineSegment(sketch, "E208.MirrorCS", {"start": v(-20, 96) * mm, "end": v(-20, 100) * mm});
            skLineSegment(sketch, "E209.MirrorCS", {"start": v(-70, 96) * mm, "end": v(-70, 100) * mm});
            skLineSegment(sketch, "E210.MirrorCS", {"start": v(-90, 96) * mm, "end": v(-90, 100) * mm});
            skLineSegment(sketch, "E211.MirrorCS", {"start": v(30, 96) * mm, "end": v(30, 100) * mm});
            skLineSegment(sketch, "E212.MirrorCS", {"start": v(-100, 96) * mm, "end": v(50, 96) * mm});
            skSolve(sketch);
        }
        {
            var Q0;
            {var subQ0=sQuery(id+"F7.wireOp",EDGE,"E190.0.2.1");Q0=makeQuery(id+"F7.imprint","IMPRINT",FACE,{"disambiguationData":[TD([[makeQuery(id+"F7.imprint","IMPRINT",EDGE,{"derivedFrom":subQ0}),-1.0]])]});}
            var Q1;
            {var subQ0=sQuery(id+"F7.wireOp",EDGE,"E186");Q1=makeQuery(id+"F7.imprint","IMPRINT",FACE,{"disambiguationData":[TD([[makeQuery(id+"F7.imprint","IMPRINT",EDGE,{"derivedFrom":subQ0}),-1.0]])]});}
            var Q2;
            {var subQ0=sQuery(id+"F7.wireOp",EDGE,"E186");Q2=makeQuery(id+"F7.imprint","IMPRINT",FACE,{"disambiguationData":[TD([[makeQuery(id+"F7.imprint","IMPRINT",EDGE,{"derivedFrom":subQ0}),1.0]])]});}
            var Q3;
            {var subQ0=sQuery(id+"F7.wireOp",EDGE,"E190.0.1.0");Q3=makeQuery(id+"F7.imprint","IMPRINT",FACE,{"disambiguationData":[TD([[makeQuery(id+"F7.imprint","IMPRINT",EDGE,{"derivedFrom":subQ0}),-1.0]])]});}
            var Q4;
            {var subQ0=sQuery(id+"F7.wireOp",EDGE,"E190.0.1.1");Q4=makeQuery(id+"F7.imprint","IMPRINT",FACE,{"disambiguationData":[TD([[makeQuery(id+"F7.imprint","IMPRINT",EDGE,{"derivedFrom":subQ0}),-1.0]])]});}
            var Q5;
            {var subQ0=sQuery(id+"F7.wireOp",EDGE,"E190.0.2.0");Q5=makeQuery(id+"F7.imprint","IMPRINT",FACE,{"disambiguationData":[TD([[makeQuery(id+"F7.imprint","IMPRINT",EDGE,{"derivedFrom":subQ0}),-1.0]])]});}
            var Q6;
            {var subQ0=sQuery(id+"F7.wireOp",EDGE,"E195.MirrorCS");Q6=makeQuery(id+"F7.imprint","IMPRINT",FACE,{"disambiguationData":[TD([[makeQuery(id+"F7.imprint","IMPRINT",EDGE,{"derivedFrom":subQ0}),-1.0]])]});}
            var Q7;
            {var subQ3=sQuery(id+"F7.wireOp",EDGE,"E194.MirrorCS");Q7=makeQuery(id+"F7.imprint","IMPRINT",FACE,{"disambiguationData":[TD([[makeQuery(id+"F7.imprint","IMPRINT",EDGE,{"derivedFrom":subQ3}),1.0]])]});}
            var Q8;
            {var subQ0=sQuery(id+"F7.wireOp",EDGE,"E194.MirrorCS");Q8=makeQuery(id+"F7.imprint","IMPRINT",FACE,{"disambiguationData":[TD([[makeQuery(id+"F7.imprint","IMPRINT",EDGE,{"derivedFrom":subQ0}),-1.0]])]});}
            var Q9;
            {var subQ0=sQuery(id+"F7.wireOp",EDGE,"E191.MirrorCS");Q9=makeQuery(id+"F7.imprint","IMPRINT",FACE,{"disambiguationData":[TD([[makeQuery(id+"F7.imprint","IMPRINT",EDGE,{"derivedFrom":subQ0}),-1.0]])]});}
            var Q10;
            {var subQ0=sQuery(id+"F7.wireOp",EDGE,"E192.MirrorCS");Q10=makeQuery(id+"F7.imprint","IMPRINT",FACE,{"disambiguationData":[TD([[makeQuery(id+"F7.imprint","IMPRINT",EDGE,{"derivedFrom":subQ0}),-1.0]])]});}
            var Q11;
            {var subQ5=sQuery(id+"F7.wireOp",EDGE,"E184");var subQ7=sQuery(id+"F7.wireOp",EDGE,"E185");var subQ8=makeQuery(id+"F7.imprint","INTERSECT",VERTEX,{"derivedFrom":[subQ5,subQ7]});var subQ21=makeQuery(id+"F7.imprint","INTERSECT",VERTEX,{"derivedFrom":[subQ5,sQuery(id+"F7.wireOp",EDGE,"E198.0")]});Q11=makeQuery(id+"F7.imprint","IMPRINT",FACE,{"disambiguationData":[TD([[makeQuery(id+"F7.imprint","IMPRINT",EDGE,{"disambiguationData":[TD([[subQ8,-1.0],[subQ21,1.0]])],"derivedFrom":subQ5}),1.0]])]});}
            var Q12;
            {var subQ0=sQuery(id+"F7.wireOp",EDGE,"E190.0.2.2");Q12=makeQuery(id+"F7.imprint","IMPRINT",FACE,{"disambiguationData":[TD([[makeQuery(id+"F7.imprint","IMPRINT",EDGE,{"derivedFrom":subQ0}),-1.0]])]});}
            var Q13;
            {var subQ0=sQuery(id+"F7.wireOp",EDGE,"E206.MirrorCS");Q13=makeQuery(id+"F7.imprint","IMPRINT",FACE,{"disambiguationData":[TD([[makeQuery(id+"F7.imprint","IMPRINT",EDGE,{"derivedFrom":subQ0}),-1.0]])]});}
            var Q14;
            {var subQ0=sQuery(id+"F7.wireOp",EDGE,"E199.MirrorCS");Q14=makeQuery(id+"F7.imprint","IMPRINT",FACE,{"disambiguationData":[TD([[makeQuery(id+"F7.imprint","IMPRINT",EDGE,{"derivedFrom":subQ0}),-1.0]])]});}
            var Q15;
            {var subQ0=sQuery(id+"F7.wireOp",EDGE,"E200.MirrorCS");Q15=makeQuery(id+"F7.imprint","IMPRINT",FACE,{"disambiguationData":[TD([[makeQuery(id+"F7.imprint","IMPRINT",EDGE,{"derivedFrom":subQ0}),1.0]])]});}
            var Q16;
            {var subQ0=sQuery(id+"F7.wireOp",EDGE,"E201.MirrorCS");Q16=makeQuery(id+"F7.imprint","IMPRINT",FACE,{"disambiguationData":[TD([[makeQuery(id+"F7.imprint","IMPRINT",EDGE,{"derivedFrom":subQ0}),1.0]])]});}
            var Q17;
            {var subQ0=sQuery(id+"F7.wireOp",EDGE,"E202.MirrorCS");Q17=makeQuery(id+"F7.imprint","IMPRINT",FACE,{"disambiguationData":[TD([[makeQuery(id+"F7.imprint","IMPRINT",EDGE,{"derivedFrom":subQ0}),1.0]])]});}
            var Q18;
            {var subQ0=sQuery(id+"F7.wireOp",EDGE,"E205.MirrorCS");Q18=makeQuery(id+"F7.imprint","IMPRINT",FACE,{"disambiguationData":[TD([[makeQuery(id+"F7.imprint","IMPRINT",EDGE,{"derivedFrom":subQ0}),-1.0]])]});}
            extrude(context, id + "F8", {"entities" : qUnion([Q0, Q1, Q2, Q3, Q4, Q5, Q6, Q7, Q8, Q9, Q10, Q11, Q12, Q13, Q14, Q15, Q16, Q17, Q18]), "oppositeDirection" : true, "depth" : 4 * mm});
        }
        {
            var Q0;
            Q0=makeQuery(id+"F8.opExtrude","SWEPT_BODY",BODY,{"disambiguationData":[OSD([sQuery(id+"F7.wireOp",EDGE,"E183.bottom"),sQuery(id+"F7.wireOp",EDGE,"E183.right"),sQuery(id+"F7.wireOp",EDGE,"E184"),sQuery(id+"F7.wireOp",EDGE,"E185"),sQuery(id+"F7.wireOp",EDGE,"E187"),sQuery(id+"F7.wireOp",EDGE,"E188"),sQuery(id+"F7.wireOp",EDGE,"E189.MirrorCS"),sQuery(id+"F7.wireOp",EDGE,"E190.0.1.0"),sQuery(id+"F7.wireOp",EDGE,"E190.0.1.2"),sQuery(id+"F7.wireOp",EDGE,"E190.0.2.0"),sQuery(id+"F7.wireOp",EDGE,"E190.0.2.2"),sQuery(id+"F7.wireOp",EDGE,"E191.MirrorCS"),sQuery(id+"F7.wireOp",EDGE,"E193.MirrorCS"),sQuery(id+"F7.wireOp",EDGE,"E196.MirrorCS")])]});
            var Q1;
            Q1=qCreatedBy(makeId("Right.planeOp"),FACE);
            mirror(context, id + "F9", {"entities" : qUnion([Q0]), "mirrorPlane" : qUnion([Q1])});
        }
        {
            var Q0;
            Q0=makeQuery(id+"F2.opExtrude","CAP_FACE",FACE,{"disambiguationData":[OSD([sQuery(id+"F0.wireOp",EDGE,"E5"),sQuery(id+"F0.wireOp",EDGE,"E79.MirrorCS"),sQuery(id+"F0.wireOp",EDGE,"E83.MirrorCS"),sQuery(id+"F0.wireOp",EDGE,"E96.MirrorCS")])],"isStart":false});
            var sketch = newSketch(context, id + "F10", { "sketchPlane" : qUnion([Q0])});
            skLineSegment(sketch, "E213", {"start": v(100, 50) * mm, "end": v(7.7, 88.46) * mm});
            skLineSegment(sketch, "E214", {"start": v(-7.7, 88.46) * mm, "end": v(-100, 50) * mm});
            skArc(sketch, "E215", {"start": v(7.7, 88.46) * mm, "mid": v(0, 90) * mm, "end": v(-7.7, 88.46) * mm});
            skLineSegment(sketch, "E216", {"start": v(7.7, 84.13) * mm, "end": v(100, 45.67) * mm});
            skLineSegment(sketch, "E217", {"start": v(-7.7, 84.13) * mm, "end": v(-100, 45.67) * mm});
            skLineSegment(sketch, "E218", {"start": v(100, 45.67) * mm, "end": v(100, 50) * mm});
            skLineSegment(sketch, "E219", {"start": v(-100, 45.67) * mm, "end": v(-100, 50) * mm});
            skLineSegment(sketch, "E220.0", {"start": v(4.62, 85.41) * mm, "end": v(-4.62, 85.41) * mm});
            skLineSegment(sketch, "E221", {"start": v(-7.7, 84.13) * mm, "end": v(-4.62, 85.41) * mm});
            skLineSegment(sketch, "E222", {"start": v(4.62, 85.41) * mm, "end": v(7.7, 84.13) * mm});
            skLineSegment(sketch, "E223.0", {"start": v(-12.3, 86.54) * mm, "end": v(-10.77, 82.85) * mm});
            skLineSegment(sketch, "E224.0", {"start": v(12.3, 86.54) * mm, "end": v(10.77, 82.85) * mm});
            skLineSegment(sketch, "E225", {"start": v(100, 50) * mm, "end": v(98.46, 46.3) * mm});
            skLineSegment(sketch, "E226", {"start": v(94.77, 47.85) * mm, "end": v(96.3, 51.54) * mm});
            skLineSegment(sketch, "E227", {"start": v(-100, 50) * mm, "end": v(-98.46, 46.3) * mm});
            skLineSegment(sketch, "E228", {"start": v(-96.3, 51.54) * mm, "end": v(-94.77, 47.85) * mm});
            skLineSegment(sketch, "E229.0", {"start": v(38.46, 71.3) * mm, "end": v(0, 87.33) * mm});
            skLineSegment(sketch, "E229.1", {"start": v(-47.7, 67.46) * mm, "end": v(0, 87.33) * mm});
            skLineSegment(sketch, "E229.2", {"start": v(0, 91.67) * mm, "end": v(21.54, 82.7) * mm});
            skLineSegment(sketch, "E229.3", {"start": v(-21.54, 82.7) * mm, "end": v(0, 91.67) * mm});
            skSolve(sketch);
        }
        {
            var Q0;
            {var subQ1=makeQuery(id+"F2.opExtrude","CAP_EDGE",EDGE,{"disambiguationData":[OSD([sQuery(id+"F0.wireOp",EDGE,"E79.MirrorCS")])],"isStart":false});Q0=makeQuery(id+"F10.imprint","IMPRINT",FACE,{"disambiguationData":[TD([[makeQuery(id+"F10.imprint","IMPRINT",EDGE,{"derivedFrom":subQ1}),1.0]])]});}
            var Q1;
            {var subQ2=sQuery(id+"F10.wireOp",EDGE,"E224.0");Q1=makeQuery(id+"F10.imprint","IMPRINT",FACE,{"disambiguationData":[TD([[makeQuery(id+"F10.imprint","IMPRINT",EDGE,{"derivedFrom":subQ2}),1.0]])]});}
            var Q2;
            Q2=makeQuery(id+"F10.imprint","IMPRINT",FACE,{"disambiguationData":[TD([[makeQuery(id+"F10.imprint","IMPRINT",EDGE,{"derivedFrom":sQuery(id+"F10.wireOp",EDGE,"c4e83639-925b-43b9-a360-e3d29ec260bf.0")}),1.0]])]});
            var Q3;
            {var subQ2=sQuery(id+"F10.wireOp",EDGE,"E226");Q3=makeQuery(id+"F10.imprint","IMPRINT",FACE,{"disambiguationData":[TD([[makeQuery(id+"F10.imprint","IMPRINT",EDGE,{"derivedFrom":subQ2}),1.0]])]});}
            var Q4;
            {var subQ0=sQuery(id+"F10.wireOp",EDGE,"E225");Q4=makeQuery(id+"F10.imprint","IMPRINT",FACE,{"disambiguationData":[TD([[makeQuery(id+"F10.imprint","IMPRINT",EDGE,{"derivedFrom":subQ0}),-1.0]])]});}
            var Q5;
            {var subQ0=sQuery(id+"F10.wireOp",EDGE,"E223.0");Q5=makeQuery(id+"F10.imprint","IMPRINT",FACE,{"disambiguationData":[TD([[makeQuery(id+"F10.imprint","IMPRINT",EDGE,{"derivedFrom":subQ0}),-1.0]])]});}
            var Q6;
            {var subQ0=sQuery(id+"F10.wireOp",EDGE,"E227");Q6=makeQuery(id+"F10.imprint","IMPRINT",FACE,{"disambiguationData":[TD([[makeQuery(id+"F10.imprint","IMPRINT",EDGE,{"derivedFrom":subQ0}),1.0]])]});}
            var Q7;
            {var subQ4=sQuery(id+"F10.wireOp",EDGE,"E215");Q7=makeQuery(id+"F10.imprint","IMPRINT",FACE,{"disambiguationData":[TD([[makeQuery(id+"F10.imprint","IMPRINT",EDGE,{"derivedFrom":subQ4}),1.0]])]});}
            var Q8;
            {var subQ0=sQuery(id+"F10.wireOp",EDGE,"E215");Q8=makeQuery(id+"F10.imprint","IMPRINT",FACE,{"disambiguationData":[TD([[makeQuery(id+"F10.imprint","IMPRINT",EDGE,{"derivedFrom":subQ0}),-1.0]])]});}
            extrude(context, id + "F11", {"entities" : qUnion([Q0, Q1, Q2, Q3, Q4, Q5, Q6, Q7, Q8]), "depth" : 46 * mm});
        }
        {
            var Q0;
            Q0=makeQuery(id+"F11.opExtrude","SWEPT_BODY",BODY,{"disambiguationData":[OSD([sQuery(id+"F10.wireOp",EDGE,"E213"),sQuery(id+"F10.wireOp",EDGE,"E214"),sQuery(id+"F10.wireOp",EDGE,"E215"),sQuery(id+"F10.wireOp",EDGE,"E216"),sQuery(id+"F10.wireOp",EDGE,"E217"),sQuery(id+"F10.wireOp",EDGE,"xkwJUleI-Cwzb-lOwz-Vpuw-UHJIeIoqi7Cv"),sQuery(id+"F10.wireOp",EDGE,"E218"),sQuery(id+"F10.wireOp",EDGE,"E219")])]});
            var Q1;
            Q1=makeQuery(id+"FW37Ere4EUHaROH_43.opExtrude","SWEPT_BODY",BODY,{"disambiguationData":[OSD([sQuery(id+"F7.wireOp",EDGE,"E183.bottom"),sQuery(id+"F7.wireOp",EDGE,"E183.right"),sQuery(id+"F7.wireOp",EDGE,"E187"),sQuery(id+"F7.wireOp",EDGE,"E190.0.2.2")])]});
            var Q2;
            Q2=makeQuery(id+"FW37Ere4EUHaROH_43.opExtrude","SWEPT_BODY",BODY,{"disambiguationData":[OSD([sQuery(id+"F7.wireOp",EDGE,"E183.right"),sQuery(id+"F7.wireOp",EDGE,"E187"),sQuery(id+"F7.wireOp",EDGE,"E190.0.1.2"),sQuery(id+"F7.wireOp",EDGE,"E190.0.2.0")])]});
            var Q3;
            Q3=makeQuery(id+"FW37Ere4EUHaROH_43.opExtrude","SWEPT_BODY",BODY,{"disambiguationData":[OSD([sQuery(id+"F7.wireOp",EDGE,"E183.right"),sQuery(id+"F7.wireOp",EDGE,"E187"),sQuery(id+"F7.wireOp",EDGE,"E188"),sQuery(id+"F7.wireOp",EDGE,"E190.0.1.0")])]});
            var Q4;
            Q4=makeQuery(id+"FW37Ere4EUHaROH_43.opExtrude","SWEPT_BODY",BODY,{"disambiguationData":[OSD([sQuery(id+"F7.wireOp",EDGE,"E183.right"),sQuery(id+"F7.wireOp",EDGE,"E187"),sQuery(id+"F7.wireOp",EDGE,"E189.MirrorCS"),sQuery(id+"F7.wireOp",EDGE,"E193.MirrorCS")])]});
            var Q5;
            Q5=makeQuery(id+"FW37Ere4EUHaROH_43.opExtrude","SWEPT_BODY",BODY,{"disambiguationData":[OSD([sQuery(id+"F7.wireOp",EDGE,"E183.right"),sQuery(id+"F7.wireOp",EDGE,"E187"),sQuery(id+"F7.wireOp",EDGE,"E191.MirrorCS"),sQuery(id+"F7.wireOp",EDGE,"E196.MirrorCS")])]});
            var Q6;
            Q6=makeQuery(id+"F2.opExtrude","SWEPT_BODY",BODY,{"disambiguationData":[OSD([sQuery(id+"F0.wireOp",EDGE,"E5"),sQuery(id+"F0.wireOp",EDGE,"E88.MirrorCS"),sQuery(id+"F0.wireOp",EDGE,"E91.MirrorCS"),sQuery(id+"F0.wireOp",EDGE,"E95.MirrorCS")])]});
            var Q7;
            Q7=makeQuery(id+"F2.opExtrude","SWEPT_BODY",BODY,{"disambiguationData":[OSD([sQuery(id+"F0.wireOp",EDGE,"E5"),sQuery(id+"F0.wireOp",EDGE,"E92.MirrorCS"),sQuery(id+"F0.wireOp",EDGE,"E93.MirrorCS"),sQuery(id+"F0.wireOp",EDGE,"E95.MirrorCS")])]});
            var Q8;
            Q8=makeQuery(id+"F2.opExtrude","SWEPT_BODY",BODY,{"disambiguationData":[OSD([sQuery(id+"F0.wireOp",EDGE,"E5"),sQuery(id+"F0.wireOp",EDGE,"E80.MirrorCS"),sQuery(id+"F0.wireOp",EDGE,"E94.MirrorCS"),sQuery(id+"F0.wireOp",EDGE,"E96.MirrorCS")])]});
            var Q9;
            Q9=makeQuery(id+"F2.opExtrude","SWEPT_BODY",BODY,{"disambiguationData":[OSD([sQuery(id+"F0.wireOp",EDGE,"E5"),sQuery(id+"F0.wireOp",EDGE,"E79.MirrorCS"),sQuery(id+"F0.wireOp",EDGE,"E83.MirrorCS"),sQuery(id+"F0.wireOp",EDGE,"E96.MirrorCS")])]});
            var Q10;
            Q10=makeQuery(id+"F2.opExtrude","SWEPT_BODY",BODY,{"disambiguationData":[OSD([sQuery(id+"F0.wireOp",EDGE,"E4"),sQuery(id+"F0.wireOp",EDGE,"E68.MirrorCS"),sQuery(id+"F0.wireOp",EDGE,"E75.MirrorCS"),sQuery(id+"F0.wireOp",EDGE,"E78.MirrorCS")])]});
            var Q11;
            Q11=makeQuery(id+"F2.opExtrude","SWEPT_BODY",BODY,{"disambiguationData":[OSD([sQuery(id+"F0.wireOp",EDGE,"E4"),sQuery(id+"F0.wireOp",EDGE,"E68.MirrorCS"),sQuery(id+"F0.wireOp",EDGE,"E70.MirrorCS"),sQuery(id+"F0.wireOp",EDGE,"E76.MirrorCS")])]});
            var Q12;
            Q12=makeQuery(id+"F2.opExtrude","SWEPT_BODY",BODY,{"disambiguationData":[OSD([sQuery(id+"F0.wireOp",EDGE,"E4"),sQuery(id+"F0.wireOp",EDGE,"E67"),sQuery(id+"F0.wireOp",EDGE,"E69"),sQuery(id+"F0.wireOp",EDGE,"E71.1.0.0")])]});
            var Q13;
            Q13=makeQuery(id+"F2.opExtrude","SWEPT_BODY",BODY,{"disambiguationData":[OSD([sQuery(id+"F0.wireOp",EDGE,"E4"),sQuery(id+"F0.wireOp",EDGE,"E67"),sQuery(id+"F0.wireOp",EDGE,"E71.1.0.1"),sQuery(id+"F0.wireOp",EDGE,"E72.0.2.0")])]});
            var Q14;
            Q14=makeQuery(id+"FSbBi1IY0pm1xVQ_48.opPattern","COPY",BODY,{"derivedFrom":makeQuery(id+"FW37Ere4EUHaROH_43.opExtrude","SWEPT_BODY",BODY,{"disambiguationData":[OSD([sQuery(id+"F7.wireOp",EDGE,"E183.bottom"),sQuery(id+"F7.wireOp",EDGE,"E183.right"),sQuery(id+"F7.wireOp",EDGE,"E187"),sQuery(id+"F7.wireOp",EDGE,"E190.0.2.2")])]}),"instanceName":"1"});
            var Q15;
            Q15=makeQuery(id+"FSbBi1IY0pm1xVQ_48.opPattern","COPY",BODY,{"derivedFrom":makeQuery(id+"FW37Ere4EUHaROH_43.opExtrude","SWEPT_BODY",BODY,{"disambiguationData":[OSD([sQuery(id+"F7.wireOp",EDGE,"E183.right"),sQuery(id+"F7.wireOp",EDGE,"E187"),sQuery(id+"F7.wireOp",EDGE,"E190.0.1.2"),sQuery(id+"F7.wireOp",EDGE,"E190.0.2.0")])]}),"instanceName":"1"});
            var Q16;
            Q16=makeQuery(id+"FSbBi1IY0pm1xVQ_48.opPattern","COPY",BODY,{"derivedFrom":makeQuery(id+"FW37Ere4EUHaROH_43.opExtrude","SWEPT_BODY",BODY,{"disambiguationData":[OSD([sQuery(id+"F7.wireOp",EDGE,"E183.right"),sQuery(id+"F7.wireOp",EDGE,"E187"),sQuery(id+"F7.wireOp",EDGE,"E188"),sQuery(id+"F7.wireOp",EDGE,"E190.0.1.0")])]}),"instanceName":"1"});
            var Q17;
            Q17=makeQuery(id+"FSbBi1IY0pm1xVQ_48.opPattern","COPY",BODY,{"derivedFrom":makeQuery(id+"FW37Ere4EUHaROH_43.opExtrude","SWEPT_BODY",BODY,{"disambiguationData":[OSD([sQuery(id+"F7.wireOp",EDGE,"E183.right"),sQuery(id+"F7.wireOp",EDGE,"E187"),sQuery(id+"F7.wireOp",EDGE,"E189.MirrorCS"),sQuery(id+"F7.wireOp",EDGE,"E193.MirrorCS")])]}),"instanceName":"1"});
            var Q18;
            Q18=makeQuery(id+"FSbBi1IY0pm1xVQ_48.opPattern","COPY",BODY,{"derivedFrom":makeQuery(id+"FW37Ere4EUHaROH_43.opExtrude","SWEPT_BODY",BODY,{"disambiguationData":[OSD([sQuery(id+"F7.wireOp",EDGE,"E183.right"),sQuery(id+"F7.wireOp",EDGE,"E187"),sQuery(id+"F7.wireOp",EDGE,"E191.MirrorCS"),sQuery(id+"F7.wireOp",EDGE,"E196.MirrorCS")])]}),"instanceName":"1"});
            var Q19;
            Q19=makeQuery(id+"F2.opExtrude","SWEPT_BODY",BODY,{"disambiguationData":[OSD([sQuery(id+"F0.wireOp",EDGE,"E2"),sQuery(id+"F0.wireOp",EDGE,"E5"),sQuery(id+"F0.wireOp",EDGE,"E85.MirrorCS"),sQuery(id+"F0.wireOp",EDGE,"E96.MirrorCS"),sQuery(id+"F0.wireOp",EDGE,"5feUKaIZ-YVe4-5bwL-nohM-rUMzkgmBEeui")])]});
            var Q20;
            Q20=makeQuery(id+"F2.opExtrude","SWEPT_BODY",BODY,{"disambiguationData":[OSD([sQuery(id+"F0.wireOp",EDGE,"E2"),sQuery(id+"F0.wireOp",EDGE,"E4"),sQuery(id+"F0.wireOp",EDGE,"E68.MirrorCS"),sQuery(id+"F0.wireOp",EDGE,"E73.MirrorCS"),sQuery(id+"F0.wireOp",EDGE,"9VRpmUI2-KmG0-2DO5-QU92-hNNclBd8RN3t")])]});
            booleanBodies(context, id + "F12", {"operationType" : BooleanOperationType.UNION, "tools" : qUnion([Q0, Q1, Q2, Q3, Q4, Q5, Q6, Q7, Q8, Q9, Q10, Q11, Q12, Q13, Q14, Q15, Q16, Q17, Q18, Q19, Q20])});
        }
        {
            var Q0;
            Q0=makeQuery(id+"F11.opExtrude","SWEPT_BODY",BODY,{"disambiguationData":[OSD([sQuery(id+"F10.wireOp",EDGE,"E213"),sQuery(id+"F10.wireOp",EDGE,"E214"),sQuery(id+"F10.wireOp",EDGE,"E215"),sQuery(id+"F10.wireOp",EDGE,"E216"),sQuery(id+"F10.wireOp",EDGE,"E217"),sQuery(id+"F10.wireOp",EDGE,"xkwJUleI-Cwzb-lOwz-Vpuw-UHJIeIoqi7Cv"),sQuery(id+"F10.wireOp",EDGE,"E218"),sQuery(id+"F10.wireOp",EDGE,"E219")])]});
            var Q1;
            Q1=makeQuery(id+"F11.opExtrude","CAP_FACE",FACE,{"disambiguationData":[OSD([sQuery(id+"F10.wireOp",EDGE,"E213"),sQuery(id+"F10.wireOp",EDGE,"E214"),sQuery(id+"F10.wireOp",EDGE,"E215"),sQuery(id+"F10.wireOp",EDGE,"E216"),sQuery(id+"F10.wireOp",EDGE,"E217"),sQuery(id+"F10.wireOp",EDGE,"xkwJUleI-Cwzb-lOwz-Vpuw-UHJIeIoqi7Cv"),sQuery(id+"F10.wireOp",EDGE,"E218"),sQuery(id+"F10.wireOp",EDGE,"E219")])],"isStart":false});
            mirror(context, id + "F13", {"entities" : qUnion([Q0]), "mirrorPlane" : qUnion([Q1])});
        }
        {
            var Q0;
            Q0=makeQuery(id+"F13.opPattern","COPY",BODY,{"derivedFrom":makeQuery(id+"F11.opExtrude","SWEPT_BODY",BODY,{"disambiguationData":[OSD([sQuery(id+"F10.wireOp",EDGE,"E213"),sQuery(id+"F10.wireOp",EDGE,"E214"),sQuery(id+"F10.wireOp",EDGE,"E215"),sQuery(id+"F10.wireOp",EDGE,"E216"),sQuery(id+"F10.wireOp",EDGE,"E217"),sQuery(id+"F10.wireOp",EDGE,"xkwJUleI-Cwzb-lOwz-Vpuw-UHJIeIoqi7Cv"),sQuery(id+"F10.wireOp",EDGE,"E218"),sQuery(id+"F10.wireOp",EDGE,"E219")])]}),"instanceName":"1"});
            var Q1;
            Q1=makeQuery(id+"F11.opExtrude","SWEPT_BODY",BODY,{"disambiguationData":[OSD([sQuery(id+"F10.wireOp",EDGE,"E213"),sQuery(id+"F10.wireOp",EDGE,"E214"),sQuery(id+"F10.wireOp",EDGE,"E215"),sQuery(id+"F10.wireOp",EDGE,"E216"),sQuery(id+"F10.wireOp",EDGE,"E217"),sQuery(id+"F10.wireOp",EDGE,"xkwJUleI-Cwzb-lOwz-Vpuw-UHJIeIoqi7Cv"),sQuery(id+"F10.wireOp",EDGE,"E218"),sQuery(id+"F10.wireOp",EDGE,"E219")])]});
            booleanBodies(context, id + "F14", {"operationType" : BooleanOperationType.UNION, "tools" : qUnion([Q0, Q1])});
        }
        {
            var Q0;
            Q0=makeQuery(id+"F1.opExtrude","SWEPT_BODY",BODY,{"disambiguationData":[OSD([sQuery(id+"F0.wireOp",EDGE,"E1.top"),sQuery(id+"F0.wireOp",EDGE,"E1.left"),sQuery(id+"F0.wireOp",EDGE,"E1.right"),sQuery(id+"F0.wireOp",EDGE,"E2"),sQuery(id+"F0.wireOp",EDGE,"E4"),sQuery(id+"F0.wireOp",EDGE,"E5"),sQuery(id+"F0.wireOp",EDGE,"E7"),sQuery(id+"F0.wireOp",EDGE,"E8"),sQuery(id+"F0.wireOp",EDGE,"E9.MirrorCS"),sQuery(id+"F0.wireOp",EDGE,"E11.0.1.1"),sQuery(id+"F0.wireOp",EDGE,"E11.0.1.2"),sQuery(id+"F0.wireOp",EDGE,"E11.0.2.1"),sQuery(id+"F0.wireOp",EDGE,"E11.0.2.2"),sQuery(id+"F0.wireOp",EDGE,"E11.0.3.2"),sQuery(id+"F0.wireOp",EDGE,"E15.MirrorCS"),sQuery(id+"F0.wireOp",EDGE,"E16.MirrorCS"),sQuery(id+"F0.wireOp",EDGE,"E17.MirrorCS"),sQuery(id+"F0.wireOp",EDGE,"E18.MirrorCS"),sQuery(id+"F0.wireOp",EDGE,"E21.MirrorCS"),sQuery(id+"F0.wireOp",EDGE,"E23.MirrorCS"),sQuery(id+"F0.wireOp",EDGE,"E25.MirrorCS"),sQuery(id+"F0.wireOp",EDGE,"E26.MirrorCS"),sQuery(id+"F0.wireOp",EDGE,"E27.MirrorCS"),sQuery(id+"F0.wireOp",EDGE,"E29.MirrorCS"),sQuery(id+"F0.wireOp",EDGE,"E32.MirrorCS"),sQuery(id+"F0.wireOp",EDGE,"E33.MirrorCS"),sQuery(id+"F0.wireOp",EDGE,"E34.MirrorCS"),sQuery(id+"F0.wireOp",EDGE,"E35.MirrorCS"),sQuery(id+"F0.wireOp",EDGE,"E38.MirrorCS"),sQuery(id+"F0.wireOp",EDGE,"E39.MirrorCS"),sQuery(id+"F0.wireOp",EDGE,"E43.MirrorCS"),sQuery(id+"F0.wireOp",EDGE,"E44.MirrorCS"),sQuery(id+"F0.wireOp",EDGE,"E49"),sQuery(id+"F0.wireOp",EDGE,"E50.MirrorCS"),sQuery(id+"F0.wireOp",EDGE,"E51"),sQuery(id+"F0.wireOp",EDGE,"E52.MirrorCS"),sQuery(id+"F0.wireOp",EDGE,"E53.1.0.0"),sQuery(id+"F0.wireOp",EDGE,"E53.1.0.2"),sQuery(id+"F0.wireOp",EDGE,"E53.2.0.0"),sQuery(id+"F0.wireOp",EDGE,"E53.2.0.2"),sQuery(id+"F0.wireOp",EDGE,"E53.3.0.0"),sQuery(id+"F0.wireOp",EDGE,"E53.3.0.2"),sQuery(id+"F0.wireOp",EDGE,"E53.4.0.0"),sQuery(id+"F0.wireOp",EDGE,"E53.4.0.2"),sQuery(id+"F0.wireOp",EDGE,"E54.MirrorCS"),sQuery(id+"F0.wireOp",EDGE,"E56.MirrorCS"),sQuery(id+"F0.wireOp",EDGE,"E57.MirrorCS"),sQuery(id+"F0.wireOp",EDGE,"E58.MirrorCS"),sQuery(id+"F0.wireOp",EDGE,"E60.MirrorCS"),sQuery(id+"F0.wireOp",EDGE,"E61.MirrorCS"),sQuery(id+"F0.wireOp",EDGE,"E62.MirrorCS"),sQuery(id+"F0.wireOp",EDGE,"E65.MirrorCS"),sQuery(id+"F0.wireOp",EDGE,"E67"),sQuery(id+"F0.wireOp",EDGE,"E68.MirrorCS"),sQuery(id+"F0.wireOp",EDGE,"E69"),sQuery(id+"F0.wireOp",EDGE,"E70.MirrorCS"),sQuery(id+"F0.wireOp",EDGE,"E71.1.0.0"),sQuery(id+"F0.wireOp",EDGE,"E71.1.0.1"),sQuery(id+"F0.wireOp",EDGE,"E72.0.2.0"),sQuery(id+"F0.wireOp",EDGE,"E75.MirrorCS"),sQuery(id+"F0.wireOp",EDGE,"E76.MirrorCS"),sQuery(id+"F0.wireOp",EDGE,"E78.MirrorCS"),sQuery(id+"F0.wireOp",EDGE,"E79.MirrorCS"),sQuery(id+"F0.wireOp",EDGE,"E80.MirrorCS"),sQuery(id+"F0.wireOp",EDGE,"E83.MirrorCS"),sQuery(id+"F0.wireOp",EDGE,"E88.MirrorCS"),sQuery(id+"F0.wireOp",EDGE,"E91.MirrorCS"),sQuery(id+"F0.wireOp",EDGE,"E92.MirrorCS"),sQuery(id+"F0.wireOp",EDGE,"E93.MirrorCS"),sQuery(id+"F0.wireOp",EDGE,"E94.MirrorCS"),sQuery(id+"F0.wireOp",EDGE,"E95.MirrorCS"),sQuery(id+"F0.wireOp",EDGE,"E96.MirrorCS")])]});
            transform(context, id + "F15", {"entities" : qUnion([Q0]), "transformType" : TransformType.TRANSLATION_3D, "dx" : 0 * mm, "dy" : 0 * mm, "dz" : 96 * mm, "makeCopy" : true});
        }
        {
            var Q0;
            Q0=makeQuery(id+"F1.opExtrude","CAP_FACE",FACE,{"disambiguationData":[OSD([sQuery(id+"F0.wireOp",EDGE,"E1.top"),sQuery(id+"F0.wireOp",EDGE,"E1.left"),sQuery(id+"F0.wireOp",EDGE,"E1.right"),sQuery(id+"F0.wireOp",EDGE,"E2"),sQuery(id+"F0.wireOp",EDGE,"E4"),sQuery(id+"F0.wireOp",EDGE,"E5"),sQuery(id+"F0.wireOp",EDGE,"E7"),sQuery(id+"F0.wireOp",EDGE,"E8"),sQuery(id+"F0.wireOp",EDGE,"E9.MirrorCS"),sQuery(id+"F0.wireOp",EDGE,"E11.0.1.1"),sQuery(id+"F0.wireOp",EDGE,"E11.0.1.2"),sQuery(id+"F0.wireOp",EDGE,"E11.0.2.1"),sQuery(id+"F0.wireOp",EDGE,"E11.0.2.2"),sQuery(id+"F0.wireOp",EDGE,"E11.0.3.2"),sQuery(id+"F0.wireOp",EDGE,"E15.MirrorCS"),sQuery(id+"F0.wireOp",EDGE,"E16.MirrorCS"),sQuery(id+"F0.wireOp",EDGE,"E17.MirrorCS"),sQuery(id+"F0.wireOp",EDGE,"E18.MirrorCS"),sQuery(id+"F0.wireOp",EDGE,"E21.MirrorCS"),sQuery(id+"F0.wireOp",EDGE,"E23.MirrorCS"),sQuery(id+"F0.wireOp",EDGE,"E25.MirrorCS"),sQuery(id+"F0.wireOp",EDGE,"E26.MirrorCS"),sQuery(id+"F0.wireOp",EDGE,"E27.MirrorCS"),sQuery(id+"F0.wireOp",EDGE,"E29.MirrorCS"),sQuery(id+"F0.wireOp",EDGE,"E32.MirrorCS"),sQuery(id+"F0.wireOp",EDGE,"E33.MirrorCS"),sQuery(id+"F0.wireOp",EDGE,"E34.MirrorCS"),sQuery(id+"F0.wireOp",EDGE,"E35.MirrorCS"),sQuery(id+"F0.wireOp",EDGE,"E38.MirrorCS"),sQuery(id+"F0.wireOp",EDGE,"E39.MirrorCS"),sQuery(id+"F0.wireOp",EDGE,"E43.MirrorCS"),sQuery(id+"F0.wireOp",EDGE,"E44.MirrorCS"),sQuery(id+"F0.wireOp",EDGE,"E49"),sQuery(id+"F0.wireOp",EDGE,"E50.MirrorCS"),sQuery(id+"F0.wireOp",EDGE,"E51"),sQuery(id+"F0.wireOp",EDGE,"E52.MirrorCS"),sQuery(id+"F0.wireOp",EDGE,"E53.1.0.0"),sQuery(id+"F0.wireOp",EDGE,"E53.1.0.2"),sQuery(id+"F0.wireOp",EDGE,"E53.2.0.0"),sQuery(id+"F0.wireOp",EDGE,"E53.2.0.2"),sQuery(id+"F0.wireOp",EDGE,"E53.3.0.0"),sQuery(id+"F0.wireOp",EDGE,"E53.3.0.2"),sQuery(id+"F0.wireOp",EDGE,"E53.4.0.0"),sQuery(id+"F0.wireOp",EDGE,"E53.4.0.2"),sQuery(id+"F0.wireOp",EDGE,"E54.MirrorCS"),sQuery(id+"F0.wireOp",EDGE,"E56.MirrorCS"),sQuery(id+"F0.wireOp",EDGE,"E57.MirrorCS"),sQuery(id+"F0.wireOp",EDGE,"E58.MirrorCS"),sQuery(id+"F0.wireOp",EDGE,"E60.MirrorCS"),sQuery(id+"F0.wireOp",EDGE,"E61.MirrorCS"),sQuery(id+"F0.wireOp",EDGE,"E62.MirrorCS"),sQuery(id+"F0.wireOp",EDGE,"E65.MirrorCS"),sQuery(id+"F0.wireOp",EDGE,"E67"),sQuery(id+"F0.wireOp",EDGE,"E68.MirrorCS"),sQuery(id+"F0.wireOp",EDGE,"E69"),sQuery(id+"F0.wireOp",EDGE,"E70.MirrorCS"),sQuery(id+"F0.wireOp",EDGE,"E71.1.0.0"),sQuery(id+"F0.wireOp",EDGE,"E71.1.0.1"),sQuery(id+"F0.wireOp",EDGE,"E72.0.2.0"),sQuery(id+"F0.wireOp",EDGE,"E75.MirrorCS"),sQuery(id+"F0.wireOp",EDGE,"E76.MirrorCS"),sQuery(id+"F0.wireOp",EDGE,"E78.MirrorCS"),sQuery(id+"F0.wireOp",EDGE,"E79.MirrorCS"),sQuery(id+"F0.wireOp",EDGE,"E80.MirrorCS"),sQuery(id+"F0.wireOp",EDGE,"E83.MirrorCS"),sQuery(id+"F0.wireOp",EDGE,"E88.MirrorCS"),sQuery(id+"F0.wireOp",EDGE,"E91.MirrorCS"),sQuery(id+"F0.wireOp",EDGE,"E92.MirrorCS"),sQuery(id+"F0.wireOp",EDGE,"E93.MirrorCS"),sQuery(id+"F0.wireOp",EDGE,"E94.MirrorCS"),sQuery(id+"F0.wireOp",EDGE,"E95.MirrorCS"),sQuery(id+"F0.wireOp",EDGE,"E96.MirrorCS")])],"isStart":false});
            var sketch = newSketch(context, id + "F16", { "sketchPlane" : qUnion([Q0])});
            skLineSegment(sketch, "E230.bottom", {"start": v(-81, -12) * mm, "end": v(-51, -12) * mm});
            skLineSegment(sketch, "E230.top", {"start": v(-81, -81) * mm, "end": v(-51, -81) * mm});
            skLineSegment(sketch, "E230.left", {"start": v(-81, -12) * mm, "end": v(-81, -81) * mm});
            skLineSegment(sketch, "E230.right", {"start": v(-51, -12) * mm, "end": v(-51, -81) * mm});
            skLineSegment(sketch, "E231.MirrorCS", {"start": v(81, -81) * mm, "end": v(51, -81) * mm});
            skLineSegment(sketch, "E232.MirrorCS", {"start": v(81, -12) * mm, "end": v(51, -12) * mm});
            skLineSegment(sketch, "E233.MirrorCS", {"start": v(81, -12) * mm, "end": v(81, -81) * mm});
            skLineSegment(sketch, "E234.MirrorCS", {"start": v(51, -12) * mm, "end": v(51, -81) * mm});
            skSolve(sketch);
        }
        {
            var Q0;
            Q0=makeQuery(id+"F16.imprint","IMPRINT",FACE,{"disambiguationData":[TD([[makeQuery(id+"F16.imprint","IMPRINT",EDGE,{"derivedFrom":sQuery(id+"F16.wireOp",EDGE,"E230.bottom")}),-1.0]])]});
            var Q1;
            Q1=makeQuery(id+"F16.imprint","IMPRINT",FACE,{"disambiguationData":[TD([[makeQuery(id+"F16.imprint","IMPRINT",EDGE,{"derivedFrom":sQuery(id+"F16.wireOp",EDGE,"E231.MirrorCS")}),-1.0]])]});
            extrude(context, id + "F17", {"entities" : qUnion([Q0, Q1]), "operationType" : NewBodyOperationType.REMOVE, "endBound" : BoundingType.THROUGH_ALL, "oppositeDirection" : true, "depth" : 25 * mm});
        }
        {
            var Q0;
            {var subQ0=sQuery(id+"F0.wireOp",EDGE,"E5");var subQ1=makeQuery(id+"F12.opBoolean","MERGE",FACE,{"derivedFrom":[makeQuery(id+"F2.opExtrude","SWEPT_FACE",FACE,{"disambiguationData":[OSD([subQ0]),TDD([makeQuery(id+"F0.imprint","IMPRINT",EDGE,{"disambiguationData":[TD([[makeQuery(id+"F0.imprint","INTERSECT",VERTEX,{"derivedFrom":[subQ0,sQuery(id+"F0.wireOp",EDGE,"E85.MirrorCS")]}),1.0]])],"derivedFrom":subQ0})])]}),makeQuery(id+"F2.opExtrude","SWEPT_FACE",FACE,{"disambiguationData":[OSD([subQ0]),TDD([makeQuery(id+"F0.imprint","IMPRINT",EDGE,{"disambiguationData":[TD([[makeQuery(id+"F0.imprint","INTERSECT",VERTEX,{"derivedFrom":[subQ0,sQuery(id+"F0.wireOp",EDGE,"E79.MirrorCS")]}),-1.0]])],"derivedFrom":subQ0})])]}),makeQuery(id+"F2.opExtrude","SWEPT_FACE",FACE,{"disambiguationData":[OSD([subQ0]),TDD([makeQuery(id+"F0.imprint","IMPRINT",EDGE,{"disambiguationData":[TD([[makeQuery(id+"F0.imprint","INTERSECT",VERTEX,{"derivedFrom":[subQ0,sQuery(id+"F0.wireOp",EDGE,"E80.MirrorCS")]}),-1.0]])],"derivedFrom":subQ0})])]}),makeQuery(id+"F2.opExtrude","SWEPT_FACE",FACE,{"disambiguationData":[OSD([subQ0]),TDD([makeQuery(id+"F0.imprint","IMPRINT",EDGE,{"disambiguationData":[TD([[makeQuery(id+"F0.imprint","INTERSECT",VERTEX,{"derivedFrom":[subQ0,sQuery(id+"F0.wireOp",EDGE,"E92.MirrorCS")]}),1.0]])],"derivedFrom":subQ0})])]}),makeQuery(id+"F2.opExtrude","SWEPT_FACE",FACE,{"disambiguationData":[OSD([subQ0]),TDD([makeQuery(id+"F0.imprint","IMPRINT",EDGE,{"disambiguationData":[TD([[makeQuery(id+"F0.imprint","INTERSECT",VERTEX,{"derivedFrom":[subQ0,sQuery(id+"F0.wireOp",EDGE,"E88.MirrorCS")]}),1.0]])],"derivedFrom":subQ0})])]}),makeQuery(id+"F11.opExtrude","SWEPT_FACE",FACE,{"disambiguationData":[OSD([sQuery(id+"F10.wireOp",EDGE,"E213")])]})]});Q0=makeQuery(id+"F14.opBoolean","MERGE",FACE,{"derivedFrom":[subQ1,makeQuery(id+"F13.opPattern","COPY",FACE,{"derivedFrom":subQ1,"instanceName":"1"})]});}
            var sketch = newSketch(context, id + "F18", { "sketchPlane" : qUnion([Q0])});
            skLineSegment(sketch, "E235", {"start": v(-73.08, 50) * mm, "end": v(-69.08, 50) * mm});
            skPoint(sketch, "E235.endSnap0", {"position": v(-73.08, 50) * mm});
            skLineSegment(sketch, "E236", {"start": v(-69.08, 4) * mm, "end": v(-69.08, 96) * mm});
            skLineSegment(sketch, "E237", {"start": v(-73.08, 45) * mm, "end": v(-69.08, 45) * mm});
            skLineSegment(sketch, "E238.MirrorCS", {"start": v(-73.08, 55) * mm, "end": v(-69.08, 55) * mm});
            skLineSegment(sketch, "E239.0.1.0", {"start": v(-73.08, 65) * mm, "end": v(-69.08, 65) * mm});
            skLineSegment(sketch, "E239.0.1.1", {"start": v(-73.08, 75) * mm, "end": v(-69.08, 75) * mm});
            skPoint(sketch, "E239.0.1.2", {"position": v(-73.08, 70) * mm});
            skLineSegment(sketch, "E239.0.1.3", {"start": v(-73.08, 70) * mm, "end": v(-69.08, 70) * mm});
            skLineSegment(sketch, "E239.0.2.0", {"start": v(-73.08, 85) * mm, "end": v(-69.08, 85) * mm});
            skLineSegment(sketch, "E239.0.2.1", {"start": v(-73.08, 95) * mm, "end": v(-69.08, 95) * mm});
            skPoint(sketch, "E239.0.2.2", {"position": v(-73.08, 90) * mm});
            skLineSegment(sketch, "E239.0.2.3", {"start": v(-73.08, 90) * mm, "end": v(-69.08, 90) * mm});
            skLineSegment(sketch, "E239.direction1", {"start": v(-73.08, 45) * mm, "end": v(-48.08, 45) * mm, "construction": true});
            skLineSegment(sketch, "E239.direction2", {"start": v(-73.08, 45) * mm, "end": v(-73.08, 65) * mm, "construction": true});
            skLineSegment(sketch, "E240.MirrorCS", {"start": v(-73.08, 10) * mm, "end": v(-69.08, 10) * mm});
            skLineSegment(sketch, "E241.MirrorCS", {"start": v(-73.08, 30) * mm, "end": v(-69.08, 30) * mm});
            skPoint(sketch, "E242.MirrorP", {"position": v(-73.08, 30) * mm});
            skLineSegment(sketch, "E243.MirrorCS", {"start": v(-73.08, 15) * mm, "end": v(-69.08, 15) * mm});
            skPoint(sketch, "E244.MirrorP", {"position": v(-73.08, 10) * mm});
            skLineSegment(sketch, "E245.MirrorCS", {"start": v(-73.08, 35) * mm, "end": v(-69.08, 35) * mm});
            skLineSegment(sketch, "E246.MirrorCS", {"start": v(-73.08, 5) * mm, "end": v(-69.08, 5) * mm});
            skLineSegment(sketch, "E247.MirrorCS", {"start": v(-73.08, 25) * mm, "end": v(-69.08, 25) * mm});
            skLineSegment(sketch, "E248", {"start": v(-69.08, 4) * mm, "end": v(35.26, 4) * mm});
            skLineSegment(sketch, "E249.bottom", {"start": v(-14.74, 45) * mm, "end": v(35.26, 45) * mm});
            skLineSegment(sketch, "E249.top", {"start": v(-14.74, 41) * mm, "end": v(35.26, 41) * mm});
            skLineSegment(sketch, "E249.left", {"start": v(-14.74, 45) * mm, "end": v(-14.74, 41) * mm});
            skLineSegment(sketch, "E249.right", {"start": v(35.26, 45) * mm, "end": v(35.26, 41) * mm});
            skSolve(sketch);
        }
        {
            var Q0;
            {var subQ7=sQuery(id+"F18.wireOp",EDGE,"E246.MirrorCS");Q0=makeQuery(id+"F18.imprint","IMPRINT",FACE,{"disambiguationData":[TD([[makeQuery(id+"F18.imprint","IMPRINT",EDGE,{"derivedFrom":subQ7}),-1.0]])]});}
            var Q1;
            {var subQ0=sQuery(id+"F18.wireOp",EDGE,"E240.MirrorCS");Q1=makeQuery(id+"F18.imprint","IMPRINT",FACE,{"disambiguationData":[TD([[makeQuery(id+"F18.imprint","IMPRINT",EDGE,{"derivedFrom":subQ0}),-1.0]])]});}
            var Q2;
            {var subQ0=sQuery(id+"F18.wireOp",EDGE,"E240.MirrorCS");Q2=makeQuery(id+"F18.imprint","IMPRINT",FACE,{"disambiguationData":[TD([[makeQuery(id+"F18.imprint","IMPRINT",EDGE,{"derivedFrom":subQ0}),1.0]])]});}
            var Q3;
            {var subQ0=sQuery(id+"F18.wireOp",EDGE,"E241.MirrorCS");Q3=makeQuery(id+"F18.imprint","IMPRINT",FACE,{"disambiguationData":[TD([[makeQuery(id+"F18.imprint","IMPRINT",EDGE,{"derivedFrom":subQ0}),-1.0]])]});}
            var Q4;
            {var subQ0=sQuery(id+"F18.wireOp",EDGE,"E241.MirrorCS");Q4=makeQuery(id+"F18.imprint","IMPRINT",FACE,{"disambiguationData":[TD([[makeQuery(id+"F18.imprint","IMPRINT",EDGE,{"derivedFrom":subQ0}),1.0]])]});}
            var Q5;
            {var subQ0=sQuery(id+"F18.wireOp",EDGE,"E235");Q5=makeQuery(id+"F18.imprint","IMPRINT",FACE,{"disambiguationData":[TD([[makeQuery(id+"F18.imprint","IMPRINT",EDGE,{"derivedFrom":subQ0}),-1.0]])]});}
            var Q6;
            {var subQ0=sQuery(id+"F18.wireOp",EDGE,"E235");Q6=makeQuery(id+"F18.imprint","IMPRINT",FACE,{"disambiguationData":[TD([[makeQuery(id+"F18.imprint","IMPRINT",EDGE,{"derivedFrom":subQ0}),1.0]])]});}
            var Q7;
            {var subQ0=sQuery(id+"F18.wireOp",EDGE,"E239.0.1.0");Q7=makeQuery(id+"F18.imprint","IMPRINT",FACE,{"disambiguationData":[TD([[makeQuery(id+"F18.imprint","IMPRINT",EDGE,{"derivedFrom":subQ0}),1.0]])]});}
            var Q8;
            {var subQ0=sQuery(id+"F18.wireOp",EDGE,"E239.0.1.1");Q8=makeQuery(id+"F18.imprint","IMPRINT",FACE,{"disambiguationData":[TD([[makeQuery(id+"F18.imprint","IMPRINT",EDGE,{"derivedFrom":subQ0}),-1.0]])]});}
            var Q9;
            {var subQ0=sQuery(id+"F18.wireOp",EDGE,"E239.0.2.0");Q9=makeQuery(id+"F18.imprint","IMPRINT",FACE,{"disambiguationData":[TD([[makeQuery(id+"F18.imprint","IMPRINT",EDGE,{"derivedFrom":subQ0}),1.0]])]});}
            var Q10;
            {var subQ0=sQuery(id+"F18.wireOp",EDGE,"E239.0.2.1");Q10=makeQuery(id+"F18.imprint","IMPRINT",FACE,{"disambiguationData":[TD([[makeQuery(id+"F18.imprint","IMPRINT",EDGE,{"derivedFrom":subQ0}),-1.0]])]});}
            var Q11;
            {var subQ7=sQuery(id+"F18.wireOp",EDGE,"E239.0.2.1");Q11=makeQuery(id+"F18.imprint","IMPRINT",FACE,{"disambiguationData":[TD([[makeQuery(id+"F18.imprint","IMPRINT",EDGE,{"derivedFrom":subQ7}),1.0]])]});}
            var Q12;
            {var subQ0=sQuery(id+"F18.wireOp",EDGE,"E239.0.2.0");Q12=makeQuery(id+"F18.imprint","IMPRINT",FACE,{"disambiguationData":[TD([[makeQuery(id+"F18.imprint","IMPRINT",EDGE,{"derivedFrom":subQ0}),1.0]])]});}
            var Q13;
            Q13=makeQuery(id+"F18.imprint","IMPRINT",FACE,{"disambiguationData":[TD([[makeQuery(id+"F18.imprint","IMPRINT",EDGE,{"derivedFrom":sQuery(id+"F18.wireOp",EDGE,"E249.bottom")}),-1.0]])]});
            extrude(context, id + "F19", {"entities" : qUnion([Q0, Q1, Q2, Q3, Q4, Q5, Q6, Q7, Q8, Q9, Q10, Q11, Q12, Q13]), "operationType" : NewBodyOperationType.REMOVE, "endBound" : BoundingType.THROUGH_ALL, "oppositeDirection" : true, "depth" : 25 * mm});
        }
        {
            var Q0;
            {var subQ0=sQuery(id+"F0.wireOp",EDGE,"E4");var subQ1=makeQuery(id+"F12.opBoolean","MERGE",FACE,{"derivedFrom":[makeQuery(id+"F2.opExtrude","SWEPT_FACE",FACE,{"disambiguationData":[OSD([subQ0]),TDD([makeQuery(id+"F0.imprint","IMPRINT",EDGE,{"disambiguationData":[TD([[makeQuery(id+"F0.imprint","INTERSECT",VERTEX,{"derivedFrom":[subQ0,sQuery(id+"F0.wireOp",EDGE,"E71.1.0.1")]}),1.0]])],"derivedFrom":subQ0})])]}),makeQuery(id+"F2.opExtrude","SWEPT_FACE",FACE,{"disambiguationData":[OSD([subQ0]),TDD([makeQuery(id+"F0.imprint","IMPRINT",EDGE,{"disambiguationData":[TD([[makeQuery(id+"F0.imprint","INTERSECT",VERTEX,{"derivedFrom":[subQ0,sQuery(id+"F0.wireOp",EDGE,"E69")]}),1.0]])],"derivedFrom":subQ0})])]}),makeQuery(id+"F2.opExtrude","SWEPT_FACE",FACE,{"disambiguationData":[OSD([subQ0]),TDD([makeQuery(id+"F0.imprint","IMPRINT",EDGE,{"disambiguationData":[TD([[makeQuery(id+"F0.imprint","INTERSECT",VERTEX,{"derivedFrom":[subQ0,sQuery(id+"F0.wireOp",EDGE,"E70.MirrorCS")]}),-1.0]])],"derivedFrom":subQ0})])]}),makeQuery(id+"F2.opExtrude","SWEPT_FACE",FACE,{"disambiguationData":[OSD([subQ0]),TDD([makeQuery(id+"F0.imprint","IMPRINT",EDGE,{"disambiguationData":[TD([[makeQuery(id+"F0.imprint","INTERSECT",VERTEX,{"derivedFrom":[subQ0,sQuery(id+"F0.wireOp",EDGE,"E75.MirrorCS")]}),-1.0]])],"derivedFrom":subQ0})])]}),makeQuery(id+"F2.opExtrude","SWEPT_FACE",FACE,{"disambiguationData":[OSD([subQ0]),TDD([makeQuery(id+"F0.imprint","IMPRINT",EDGE,{"disambiguationData":[TD([[makeQuery(id+"F0.imprint","INTERSECT",VERTEX,{"derivedFrom":[subQ0,sQuery(id+"F0.wireOp",EDGE,"E73.MirrorCS")]}),-1.0]])],"derivedFrom":subQ0})])]}),makeQuery(id+"F11.opExtrude","SWEPT_FACE",FACE,{"disambiguationData":[OSD([sQuery(id+"F10.wireOp",EDGE,"E214")])]})]});Q0=makeQuery(id+"F14.opBoolean","MERGE",FACE,{"derivedFrom":[subQ1,makeQuery(id+"F13.opPattern","COPY",FACE,{"derivedFrom":subQ1,"instanceName":"1"})]});}
            var sketch = newSketch(context, id + "F20", { "sketchPlane" : qUnion([Q0])});
            skLineSegment(sketch, "E250", {"start": v(73.08, 50) * mm, "end": v(69.08, 50) * mm});
            skPoint(sketch, "E250.endSnap0", {"position": v(73.08, 50) * mm});
            skLineSegment(sketch, "E251", {"start": v(69.08, 96) * mm, "end": v(69.08, 4) * mm});
            skLineSegment(sketch, "E252", {"start": v(73.08, 55) * mm, "end": v(69.08, 55) * mm});
            skLineSegment(sketch, "E253.MirrorCS", {"start": v(73.08, 45) * mm, "end": v(69.08, 45) * mm});
            skPoint(sketch, "E254.0.1.0", {"position": v(73.08, 70) * mm});
            skLineSegment(sketch, "E254.0.1.1", {"start": v(73.08, 75) * mm, "end": v(69.08, 75) * mm});
            skLineSegment(sketch, "E254.0.1.2", {"start": v(73.08, 70) * mm, "end": v(69.08, 70) * mm});
            skLineSegment(sketch, "E254.0.1.3", {"start": v(73.08, 65) * mm, "end": v(69.08, 65) * mm});
            skPoint(sketch, "E254.0.2.0", {"position": v(73.08, 90) * mm});
            skLineSegment(sketch, "E254.0.2.1", {"start": v(73.08, 95) * mm, "end": v(69.08, 95) * mm});
            skLineSegment(sketch, "E254.0.2.2", {"start": v(73.08, 90) * mm, "end": v(69.08, 90) * mm});
            skLineSegment(sketch, "E254.0.2.3", {"start": v(73.08, 85) * mm, "end": v(69.08, 85) * mm});
            skLineSegment(sketch, "E254.direction1", {"start": v(69.08, 45) * mm, "end": v(94.08, 45) * mm, "construction": true});
            skLineSegment(sketch, "E254.direction2", {"start": v(69.08, 45) * mm, "end": v(69.08, 65) * mm, "construction": true});
            skLineSegment(sketch, "E255.MirrorCS", {"start": v(73.08, 10) * mm, "end": v(69.08, 10) * mm});
            skPoint(sketch, "E256.MirrorP", {"position": v(73.08, 10) * mm});
            skLineSegment(sketch, "E257.MirrorCS", {"start": v(73.08, 5) * mm, "end": v(69.08, 5) * mm});
            skLineSegment(sketch, "E258.MirrorCS", {"start": v(73.08, 35) * mm, "end": v(69.08, 35) * mm});
            skLineSegment(sketch, "E259.MirrorCS", {"start": v(73.08, 30) * mm, "end": v(69.08, 30) * mm});
            skLineSegment(sketch, "E260.MirrorCS", {"start": v(73.08, 15) * mm, "end": v(69.08, 15) * mm});
            skPoint(sketch, "E261.MirrorP", {"position": v(73.08, 30) * mm});
            skLineSegment(sketch, "E262.MirrorCS", {"start": v(73.08, 25) * mm, "end": v(69.08, 25) * mm});
            skLineSegment(sketch, "E263", {"start": v(69.08, 4) * mm, "end": v(-35.26, 4) * mm});
            skLineSegment(sketch, "E264.bottom", {"start": v(14.74, 45) * mm, "end": v(-35.26, 45) * mm});
            skLineSegment(sketch, "E264.top", {"start": v(14.74, 41) * mm, "end": v(-35.26, 41) * mm});
            skLineSegment(sketch, "E264.left", {"start": v(14.74, 45) * mm, "end": v(14.74, 41) * mm});
            skLineSegment(sketch, "E264.right", {"start": v(-35.26, 45) * mm, "end": v(-35.26, 41) * mm});
            skSolve(sketch);
        }
        {
            var Q0;
            Q0 = qSketchRegion(id + "F20", true);
            var Q1;
            {var subQ0=sQuery(id+"F20.wireOp",EDGE,"E254.0.1.2");Q1=makeQuery(id+"F20.imprint","IMPRINT",FACE,{"disambiguationData":[TD([[makeQuery(id+"F20.imprint","IMPRINT",EDGE,{"derivedFrom":subQ0}),1.0]])]});}
            var Q2;
            {var subQ0=sQuery(id+"F20.wireOp",EDGE,"E254.0.1.1");Q2=makeQuery(id+"F20.imprint","IMPRINT",FACE,{"disambiguationData":[TD([[makeQuery(id+"F20.imprint","IMPRINT",EDGE,{"derivedFrom":subQ0}),1.0]])]});}
            var Q3;
            {var subQ0=sQuery(id+"F20.wireOp",EDGE,"E254.0.2.2");Q3=makeQuery(id+"F20.imprint","IMPRINT",FACE,{"disambiguationData":[TD([[makeQuery(id+"F20.imprint","IMPRINT",EDGE,{"derivedFrom":subQ0}),1.0]])]});}
            var Q4;
            {var subQ0=sQuery(id+"F20.wireOp",EDGE,"E254.0.2.1");Q4=makeQuery(id+"F20.imprint","IMPRINT",FACE,{"disambiguationData":[TD([[makeQuery(id+"F20.imprint","IMPRINT",EDGE,{"derivedFrom":subQ0}),1.0]])]});}
            var Q5;
            {var subQ0=sQuery(id+"F20.wireOp",EDGE,"E250");Q5=makeQuery(id+"F20.imprint","IMPRINT",FACE,{"disambiguationData":[TD([[makeQuery(id+"F20.imprint","IMPRINT",EDGE,{"derivedFrom":subQ0}),-1.0]])]});}
            var Q6;
            {var subQ0=sQuery(id+"F20.wireOp",EDGE,"E250");Q6=makeQuery(id+"F20.imprint","IMPRINT",FACE,{"disambiguationData":[TD([[makeQuery(id+"F20.imprint","IMPRINT",EDGE,{"derivedFrom":subQ0}),1.0]])]});}
            var Q7;
            {var subQ0=sQuery(id+"F20.wireOp",EDGE,"E258.MirrorCS");Q7=makeQuery(id+"F20.imprint","IMPRINT",FACE,{"disambiguationData":[TD([[makeQuery(id+"F20.imprint","IMPRINT",EDGE,{"derivedFrom":subQ0}),1.0]])]});}
            var Q8;
            {var subQ0=sQuery(id+"F20.wireOp",EDGE,"E259.MirrorCS");Q8=makeQuery(id+"F20.imprint","IMPRINT",FACE,{"disambiguationData":[TD([[makeQuery(id+"F20.imprint","IMPRINT",EDGE,{"derivedFrom":subQ0}),1.0]])]});}
            var Q9;
            {var subQ0=sQuery(id+"F20.wireOp",EDGE,"E255.MirrorCS");Q9=makeQuery(id+"F20.imprint","IMPRINT",FACE,{"disambiguationData":[TD([[makeQuery(id+"F20.imprint","IMPRINT",EDGE,{"derivedFrom":subQ0}),-1.0]])]});}
            var Q10;
            {var subQ0=sQuery(id+"F20.wireOp",EDGE,"E255.MirrorCS");Q10=makeQuery(id+"F20.imprint","IMPRINT",FACE,{"disambiguationData":[TD([[makeQuery(id+"F20.imprint","IMPRINT",EDGE,{"derivedFrom":subQ0}),1.0]])]});}
            var Q11;
            {var subQ7=sQuery(id+"F20.wireOp",EDGE,"E257.MirrorCS");Q11=makeQuery(id+"F20.imprint","IMPRINT",FACE,{"disambiguationData":[TD([[makeQuery(id+"F20.imprint","IMPRINT",EDGE,{"derivedFrom":subQ7}),1.0]])]});}
            var Q12;
            {var subQ7=sQuery(id+"F20.wireOp",EDGE,"E254.0.2.1");Q12=makeQuery(id+"F20.imprint","IMPRINT",FACE,{"disambiguationData":[TD([[makeQuery(id+"F20.imprint","IMPRINT",EDGE,{"derivedFrom":subQ7}),-1.0]])]});}
            extrude(context, id + "F21", {"entities" : qUnion([Q0, Q1, Q2, Q3, Q4, Q5, Q6, Q7, Q8, Q9, Q10, Q11, Q12]), "operationType" : NewBodyOperationType.REMOVE, "endBound" : BoundingType.THROUGH_ALL, "oppositeDirection" : true, "depth" : 25 * mm});
        }
        {
            var Q0;
            Q0=makeQuery(id+"F13.opPattern","COPY",BODY,{"derivedFrom":makeQuery(id+"F11.opExtrude","SWEPT_BODY",BODY,{"disambiguationData":[OSD([sQuery(id+"F10.wireOp",EDGE,"E213"),sQuery(id+"F10.wireOp",EDGE,"E214"),sQuery(id+"F10.wireOp",EDGE,"E216"),sQuery(id+"F10.wireOp",EDGE,"E217"),sQuery(id+"F10.wireOp",EDGE,"E225"),sQuery(id+"F10.wireOp",EDGE,"E227"),sQuery(id+"F10.wireOp",EDGE,"E229.0"),sQuery(id+"F10.wireOp",EDGE,"E229.1"),sQuery(id+"F10.wireOp",EDGE,"E229.2"),sQuery(id+"F10.wireOp",EDGE,"E229.3")])]}),"instanceName":"1"});
            transform(context, id + "F22", {"entities" : qUnion([Q0]), "transformType" : TransformType.TRANSLATION_3D, "dx" : 0 * mm, "dy" : 140 * mm, "dz" : 0 * mm, "makeCopy" : true});
        }
        {
            var Q0;
            {var subQ0=sQuery(id+"F0.wireOp",EDGE,"E4");var subQ1=makeQuery(id+"F12.opBoolean","MERGE",FACE,{"derivedFrom":[makeQuery(id+"F2.opExtrude","SWEPT_FACE",FACE,{"disambiguationData":[OSD([subQ0]),TDD([makeQuery(id+"F0.imprint","IMPRINT",EDGE,{"disambiguationData":[TD([[makeQuery(id+"F0.imprint","INTERSECT",VERTEX,{"derivedFrom":[subQ0,sQuery(id+"F0.wireOp",EDGE,"E71.1.0.1")]}),1.0]])],"derivedFrom":subQ0})])]}),makeQuery(id+"F2.opExtrude","SWEPT_FACE",FACE,{"disambiguationData":[OSD([subQ0]),TDD([makeQuery(id+"F0.imprint","IMPRINT",EDGE,{"disambiguationData":[TD([[makeQuery(id+"F0.imprint","INTERSECT",VERTEX,{"derivedFrom":[subQ0,sQuery(id+"F0.wireOp",EDGE,"E69")]}),1.0]])],"derivedFrom":subQ0})])]}),makeQuery(id+"F2.opExtrude","SWEPT_FACE",FACE,{"disambiguationData":[OSD([subQ0]),TDD([makeQuery(id+"F0.imprint","IMPRINT",EDGE,{"disambiguationData":[TD([[makeQuery(id+"F0.imprint","INTERSECT",VERTEX,{"derivedFrom":[subQ0,sQuery(id+"F0.wireOp",EDGE,"E70.MirrorCS")]}),-1.0]])],"derivedFrom":subQ0})])]}),makeQuery(id+"F2.opExtrude","SWEPT_FACE",FACE,{"disambiguationData":[OSD([subQ0]),TDD([makeQuery(id+"F0.imprint","IMPRINT",EDGE,{"disambiguationData":[TD([[makeQuery(id+"F0.imprint","INTERSECT",VERTEX,{"derivedFrom":[subQ0,sQuery(id+"F0.wireOp",EDGE,"E75.MirrorCS")]}),-1.0]])],"derivedFrom":subQ0})])]}),makeQuery(id+"F11.opExtrude","SWEPT_FACE",FACE,{"disambiguationData":[OSD([sQuery(id+"F10.wireOp",EDGE,"E214"),sQuery(id+"F10.wireOp",EDGE,"E229.3")])]})]});Q0=makeQuery(id+"F22.opPattern","COPY",FACE,{"derivedFrom":makeQuery(id+"F14.opBoolean","MERGE",FACE,{"derivedFrom":[subQ1,makeQuery(id+"F13.opPattern","COPY",FACE,{"derivedFrom":subQ1,"instanceName":"1"})]}),"instanceName":"1"});}
            extrude(context, id + "F23", {"entities" : qUnion([Q0]), "operationType" : NewBodyOperationType.REMOVE, "endBound" : BoundingType.THROUGH_ALL, "oppositeDirection" : true, "depth" : 25 * mm});
        }
    });
